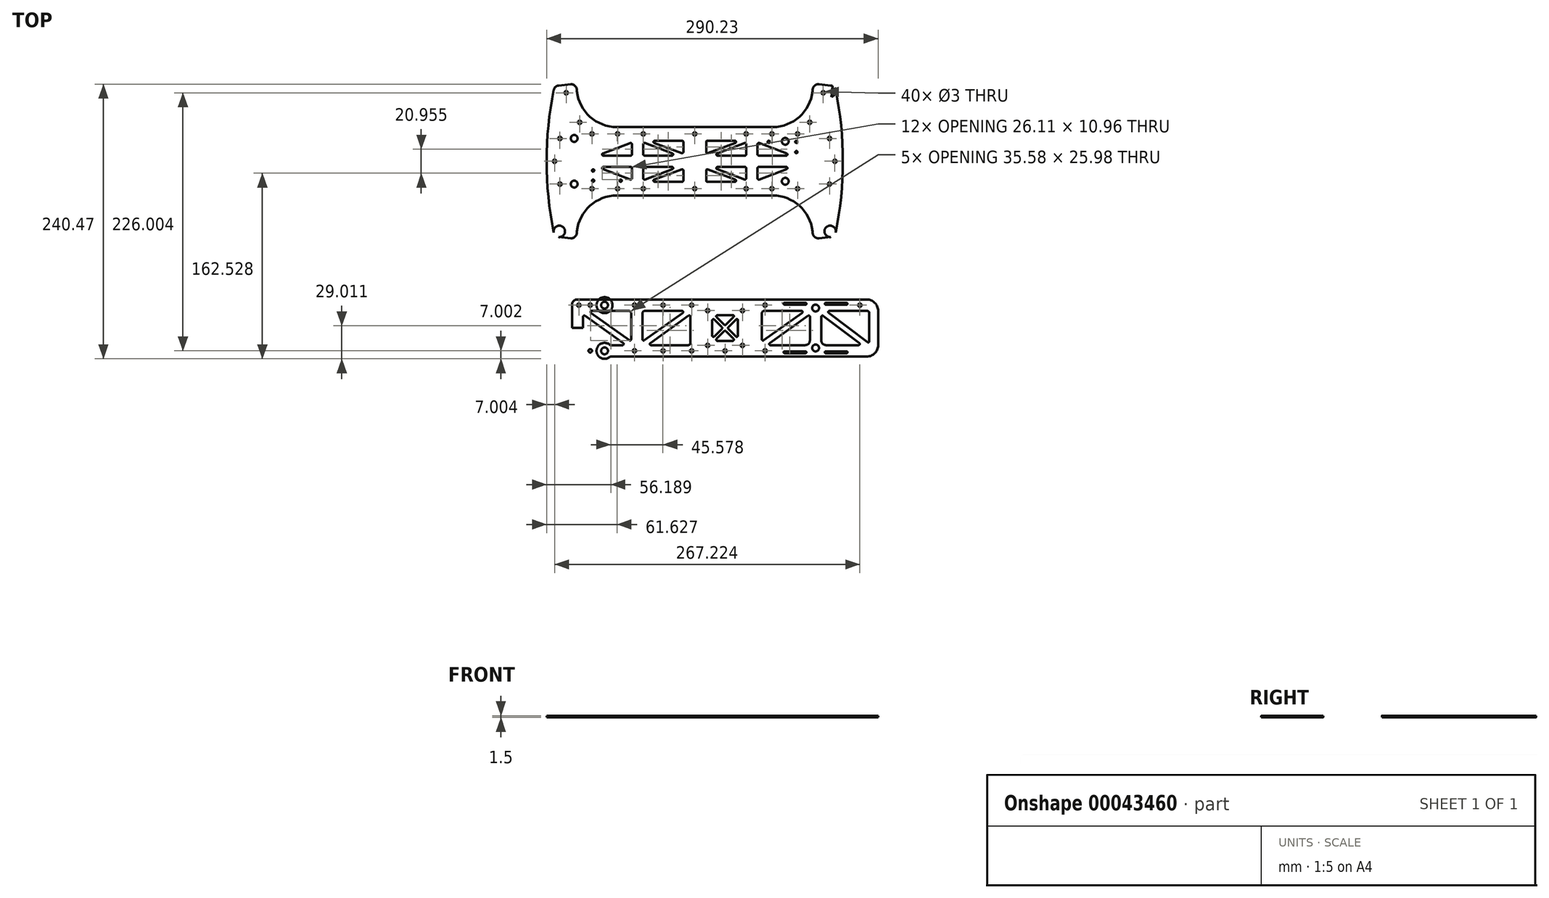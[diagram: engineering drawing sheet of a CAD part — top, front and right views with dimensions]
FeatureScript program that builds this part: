
annotation { "Feature Type Name" : "Feature", "Feature Type Description" : "" }
export const myFeature = defineFeature(function(context is Context, id is Id, definition is map)
    precondition{}
    {
        {
            var Q0;
            Q0=qCreatedBy(makeId("Top.planeOp"),FACE);
            var sketch = newSketch(context, id + "F0", { "sketchPlane" : qUnion([Q0])});
            skLineSegment(sketch, "E0", {"start": v(-133.26, 711.65) * mm, "end": v(112.1, 711.65) * mm});
            skCircle(sketch, "E1", {"center": v(-123.08, 771.65) * mm, "radius": 1.5 * mm});
            skCircle(sketch, "E2", {"center": v(-111.3, 745.73) * mm, "radius": 1.5 * mm});
            skCircle(sketch, "E3", {"center": v(90.15, 745.73) * mm, "radius": 1.5 * mm});
            skCircle(sketch, "E4", {"center": v(101.92, 771.65) * mm, "radius": 1.5 * mm});
            skLineSegment(sketch, "E5", {"start": v(-126.98, 737.05) * mm, "end": v(-131.27, 777.82) * mm});
            skLineSegment(sketch, "E6", {"start": v(-131.27, 777.82) * mm, "end": v(-116.35, 779.4) * mm});
            skLineSegment(sketch, "E7", {"start": v(-116.35, 779.4) * mm, "end": v(-112.06, 738.62) * mm});
            skLineSegment(sketch, "E8", {"start": v(-112.06, 738.62) * mm, "end": v(-126.98, 737.05) * mm});
            skLineSegment(sketch, "E9", {"start": v(-133.26, 777.61) * mm, "end": v(-119.33, 779.08) * mm});
            skLineSegment(sketch, "E10", {"start": v(-133.26, 777.61) * mm, "end": v(-133.26, 711.65) * mm});
            skLineSegment(sketch, "E11", {"start": v(95.2, 779.4) * mm, "end": v(110.11, 777.82) * mm});
            skLineSegment(sketch, "E12", {"start": v(110.11, 777.82) * mm, "end": v(105.83, 737.05) * mm});
            skLineSegment(sketch, "E13", {"start": v(105.83, 737.05) * mm, "end": v(90.91, 738.62) * mm});
            skLineSegment(sketch, "E14", {"start": v(90.91, 738.62) * mm, "end": v(95.2, 779.4) * mm});
            skLineSegment(sketch, "E15", {"start": v(98.18, 779.08) * mm, "end": v(112.1, 777.61) * mm});
            skLineSegment(sketch, "E16", {"start": v(112.1, 777.61) * mm, "end": v(112.1, 711.65) * mm});
            skLineSegment(sketch, "E17", {"start": v(-78.86, 741.65) * mm, "end": v(57.7, 741.65) * mm});
            skLineSegment(sketch, "E18", {"start": v(-113.84, 774.63) * mm, "end": v(-113.66, 772.99) * mm});
            skLineSegment(sketch, "E19", {"start": v(92.69, 774.63) * mm, "end": v(92.51, 772.99) * mm});
            skPoint(sketch, "E20.visualSharp", {"position": v(-110.37, 741.65) * mm});
            skArc(sketch, "E20.filletArc", {"start": v(-113.66, 772.99) * mm, "mid": v(-102.28, 750.64) * mm, "end": v(-78.86, 741.65) * mm});
            skPoint(sketch, "E21.visualSharp", {"position": v(89.22, 741.65) * mm});
            skArc(sketch, "E21.filletArc", {"start": v(57.7, 741.65) * mm, "mid": v(81.12, 750.64) * mm, "end": v(92.51, 772.99) * mm});
            skLineSegment(sketch, "E22.MirrorCS", {"start": v(-131.27, 645.47) * mm, "end": v(-116.35, 643.9) * mm});
            skLineSegment(sketch, "E23.MirrorCS", {"start": v(92.69, 648.66) * mm, "end": v(92.51, 650.3) * mm});
            skLineSegment(sketch, "E24.MirrorCS", {"start": v(-113.84, 648.66) * mm, "end": v(-113.66, 650.3) * mm});
            skLineSegment(sketch, "E25.MirrorCS", {"start": v(-133.26, 645.68) * mm, "end": v(-119.33, 644.21) * mm});
            skCircle(sketch, "E26.MirrorC", {"center": v(-123.08, 651.65) * mm, "radius": 1.5 * mm});
            skCircle(sketch, "E27.MirrorC", {"center": v(90.15, 677.56) * mm, "radius": 1.5 * mm});
            skCircle(sketch, "E28.MirrorC", {"center": v(-111.3, 677.56) * mm, "radius": 1.5 * mm});
            skLineSegment(sketch, "E29.MirrorCS", {"start": v(98.18, 644.21) * mm, "end": v(112.1, 645.68) * mm});
            skCircle(sketch, "E30.MirrorC", {"center": v(101.92, 651.65) * mm, "radius": 1.5 * mm});
            skPoint(sketch, "E31.MirrorP", {"position": v(-110.37, 681.65) * mm});
            skPoint(sketch, "E32.MirrorP", {"position": v(89.22, 681.65) * mm});
            skLineSegment(sketch, "E33.MirrorCS", {"start": v(110.11, 645.47) * mm, "end": v(105.83, 686.24) * mm});
            skLineSegment(sketch, "E34.MirrorCS", {"start": v(95.2, 643.9) * mm, "end": v(110.11, 645.47) * mm});
            skLineSegment(sketch, "E35.MirrorCS", {"start": v(-133.26, 645.68) * mm, "end": v(-133.26, 711.65) * mm});
            skLineSegment(sketch, "E36.MirrorCS", {"start": v(90.91, 684.68) * mm, "end": v(95.2, 643.9) * mm});
            skLineSegment(sketch, "E37.MirrorCS", {"start": v(-126.98, 686.24) * mm, "end": v(-131.27, 645.47) * mm});
            skLineSegment(sketch, "E38.MirrorCS", {"start": v(-78.86, 681.65) * mm, "end": v(57.7, 681.65) * mm});
            skLineSegment(sketch, "E39.MirrorCS", {"start": v(-116.35, 643.9) * mm, "end": v(-112.06, 684.68) * mm});
            skArc(sketch, "E40.MirrorCS", {"start": v(57.7, 681.65) * mm, "mid": v(81.12, 672.66) * mm, "end": v(92.51, 650.3) * mm});
            skLineSegment(sketch, "E41.MirrorCS", {"start": v(105.83, 686.24) * mm, "end": v(90.91, 684.68) * mm});
            skLineSegment(sketch, "E42.MirrorCS", {"start": v(-112.06, 684.68) * mm, "end": v(-126.98, 686.24) * mm});
            skLineSegment(sketch, "E43.MirrorCS", {"start": v(112.1, 645.68) * mm, "end": v(112.1, 711.65) * mm});
            skLineSegment(sketch, "E44", {"start": v(-10.58, 741.65) * mm, "end": v(-10.58, 681.65) * mm});
            skPoint(sketch, "E45.visualSharp", {"position": v(-133.26, 777.61) * mm});
            skPoint(sketch, "E46.visualSharp", {"position": v(-114.36, 779.6) * mm});
            skArc(sketch, "E46.filletArc", {"start": v(-113.84, 774.63) * mm, "mid": v(-115.66, 778) * mm, "end": v(-119.33, 779.08) * mm});
            skPoint(sketch, "E47.visualSharp", {"position": v(93.2, 779.6) * mm});
            skArc(sketch, "E47.filletArc", {"start": v(98.18, 779.08) * mm, "mid": v(94.51, 778) * mm, "end": v(92.69, 774.63) * mm});
            skPoint(sketch, "E48.visualSharp", {"position": v(112.1, 777.61) * mm});
            skPoint(sketch, "E49.visualSharp", {"position": v(-133.26, 645.68) * mm});
            skPoint(sketch, "E50.visualSharp", {"position": v(-114.36, 643.7) * mm});
            skArc(sketch, "E50.filletArc", {"start": v(-119.33, 644.21) * mm, "mid": v(-115.66, 645.3) * mm, "end": v(-113.84, 648.66) * mm});
            skPoint(sketch, "E51.visualSharp", {"position": v(93.2, 643.7) * mm});
            skArc(sketch, "E51.filletArc", {"start": v(92.69, 648.66) * mm, "mid": v(94.51, 645.3) * mm, "end": v(98.18, 644.21) * mm});
            skPoint(sketch, "E52.visualSharp", {"position": v(112.1, 645.68) * mm});
            skLineSegment(sketch, "E53", {"start": v(-122.32, 682.74) * mm, "end": v(-117.35, 682.21) * mm});
            skLineSegment(sketch, "E54", {"start": v(-115.57, 680.02) * mm, "end": v(-117.5, 661.62) * mm});
            skLineSegment(sketch, "E55", {"start": v(-119.7, 659.84) * mm, "end": v(-124.67, 660.36) * mm});
            skLineSegment(sketch, "E56", {"start": v(-126.45, 662.56) * mm, "end": v(-124.52, 680.96) * mm});
            skLineSegment(sketch, "E57.MirrorCS", {"start": v(101.17, 682.74) * mm, "end": v(96.2, 682.21) * mm});
            skLineSegment(sketch, "E58.MirrorCS", {"start": v(105.3, 662.56) * mm, "end": v(103.37, 680.96) * mm});
            skLineSegment(sketch, "E59.MirrorCS", {"start": v(98.55, 659.84) * mm, "end": v(103.52, 660.36) * mm});
            skLineSegment(sketch, "E60.MirrorCS", {"start": v(94.42, 680.02) * mm, "end": v(96.35, 661.62) * mm});
            skLineSegment(sketch, "E61.MirrorCS", {"start": v(101.17, 740.55) * mm, "end": v(96.2, 741.08) * mm});
            skLineSegment(sketch, "E62.MirrorCS", {"start": v(94.42, 743.27) * mm, "end": v(96.35, 761.67) * mm});
            skLineSegment(sketch, "E63.MirrorCS", {"start": v(105.3, 760.73) * mm, "end": v(103.37, 742.33) * mm});
            skLineSegment(sketch, "E64.MirrorCS", {"start": v(98.55, 763.45) * mm, "end": v(103.52, 762.93) * mm});
            skLineSegment(sketch, "E65.MirrorCS", {"start": v(-122.32, 740.55) * mm, "end": v(-117.35, 741.08) * mm});
            skLineSegment(sketch, "E66.MirrorCS", {"start": v(-126.45, 760.73) * mm, "end": v(-124.52, 742.33) * mm});
            skLineSegment(sketch, "E67.MirrorCS", {"start": v(-115.57, 743.27) * mm, "end": v(-117.5, 761.67) * mm});
            skLineSegment(sketch, "E68.MirrorCS", {"start": v(-119.7, 763.45) * mm, "end": v(-124.67, 762.93) * mm});
            skCircle(sketch, "E69", {"center": v(-10.58, 735.65) * mm, "radius": 1.5 * mm});
            skCircle(sketch, "E70", {"center": v(-55.58, 735.65) * mm, "radius": 1.5 * mm});
            skCircle(sketch, "E71", {"center": v(-100.58, 735.65) * mm, "radius": 1.5 * mm});
            skCircle(sketch, "E72.MirrorC", {"center": v(34.42, 735.65) * mm, "radius": 1.5 * mm});
            skCircle(sketch, "E73.MirrorC", {"center": v(79.42, 735.65) * mm, "radius": 1.5 * mm});
            skCircle(sketch, "E74.MirrorC", {"center": v(-55.58, 687.65) * mm, "radius": 1.5 * mm});
            skCircle(sketch, "E75.MirrorC", {"center": v(-10.58, 687.65) * mm, "radius": 1.5 * mm});
            skCircle(sketch, "E76.MirrorC", {"center": v(34.42, 687.65) * mm, "radius": 1.5 * mm});
            skCircle(sketch, "E77.MirrorC", {"center": v(79.42, 687.65) * mm, "radius": 1.5 * mm});
            skCircle(sketch, "E78.MirrorC", {"center": v(-100.58, 687.65) * mm, "radius": 1.5 * mm});
            skCircle(sketch, "E79", {"center": v(-133.26, 711.65) * mm, "radius": 1.5 * mm});
            skCircle(sketch, "E80.MirrorC", {"center": v(112.1, 711.65) * mm, "radius": 1.5 * mm});
            skCircle(sketch, "E81", {"center": v(-128.58, 731.65) * mm, "radius": 1.5 * mm});
            skCircle(sketch, "E82.MirrorC", {"center": v(-128.58, 691.65) * mm, "radius": 1.5 * mm});
            skCircle(sketch, "E83.MirrorC", {"center": v(107.42, 731.65) * mm, "radius": 1.5 * mm});
            skCircle(sketch, "E84.MirrorC", {"center": v(107.42, 691.65) * mm, "radius": 1.5 * mm});
            skLineSegment(sketch, "E85.bottom", {"start": v(-20.58, 716.65) * mm, "end": v(-55.58, 716.65) * mm});
            skLineSegment(sketch, "E85.top", {"start": v(-20.58, 729.65) * mm, "end": v(-55.58, 729.65) * mm});
            skLineSegment(sketch, "E85.left", {"start": v(-20.58, 716.65) * mm, "end": v(-20.58, 729.65) * mm});
            skLineSegment(sketch, "E85.right", {"start": v(-55.58, 716.65) * mm, "end": v(-55.58, 729.65) * mm});
            skLineSegment(sketch, "E86.bottom", {"start": v(-65.58, 716.65) * mm, "end": v(-100.58, 716.65) * mm});
            skLineSegment(sketch, "E86.top", {"start": v(-65.58, 729.65) * mm, "end": v(-100.58, 729.65) * mm});
            skLineSegment(sketch, "E86.left", {"start": v(-65.58, 716.65) * mm, "end": v(-65.58, 729.65) * mm});
            skLineSegment(sketch, "E86.right", {"start": v(-100.58, 716.65) * mm, "end": v(-100.58, 729.65) * mm});
            skLineSegment(sketch, "E87.MirrorCS", {"start": v(44.42, 716.65) * mm, "end": v(79.42, 716.65) * mm});
            skLineSegment(sketch, "E88.MirrorCS", {"start": v(-0.58, 716.65) * mm, "end": v(-0.58, 729.65) * mm});
            skLineSegment(sketch, "E89.MirrorCS", {"start": v(-0.58, 729.65) * mm, "end": v(34.42, 729.65) * mm});
            skLineSegment(sketch, "E90.MirrorCS", {"start": v(-0.58, 716.65) * mm, "end": v(34.42, 716.65) * mm});
            skLineSegment(sketch, "E91.MirrorCS", {"start": v(44.42, 729.65) * mm, "end": v(79.42, 729.65) * mm});
            skLineSegment(sketch, "E92.MirrorCS", {"start": v(34.42, 716.65) * mm, "end": v(34.42, 729.65) * mm});
            skLineSegment(sketch, "E93.MirrorCS", {"start": v(44.42, 716.65) * mm, "end": v(44.42, 729.65) * mm});
            skLineSegment(sketch, "E94.MirrorCS", {"start": v(79.42, 716.65) * mm, "end": v(79.42, 729.65) * mm});
            skLineSegment(sketch, "E95.MirrorCS", {"start": v(-65.58, 706.65) * mm, "end": v(-100.58, 706.65) * mm});
            skLineSegment(sketch, "E96.MirrorCS", {"start": v(-20.58, 706.65) * mm, "end": v(-55.58, 706.65) * mm});
            skLineSegment(sketch, "E97.MirrorCS", {"start": v(-20.58, 693.65) * mm, "end": v(-55.58, 693.65) * mm});
            skLineSegment(sketch, "E98.MirrorCS", {"start": v(-20.58, 706.65) * mm, "end": v(-20.58, 693.65) * mm});
            skLineSegment(sketch, "E99.MirrorCS", {"start": v(-55.58, 706.65) * mm, "end": v(-55.58, 693.65) * mm});
            skLineSegment(sketch, "E100.MirrorCS", {"start": v(-65.58, 693.65) * mm, "end": v(-100.58, 693.65) * mm});
            skLineSegment(sketch, "E101.MirrorCS", {"start": v(-65.58, 706.65) * mm, "end": v(-65.58, 693.65) * mm});
            skLineSegment(sketch, "E102.MirrorCS", {"start": v(-100.58, 706.65) * mm, "end": v(-100.58, 693.65) * mm});
            skLineSegment(sketch, "E103.MirrorCS", {"start": v(79.42, 706.65) * mm, "end": v(79.42, 693.65) * mm});
            skLineSegment(sketch, "E104.MirrorCS", {"start": v(-0.58, 706.65) * mm, "end": v(34.42, 706.65) * mm});
            skLineSegment(sketch, "E105.MirrorCS", {"start": v(44.42, 706.65) * mm, "end": v(44.42, 693.65) * mm});
            skLineSegment(sketch, "E106.MirrorCS", {"start": v(-0.58, 693.65) * mm, "end": v(34.42, 693.65) * mm});
            skLineSegment(sketch, "E107.MirrorCS", {"start": v(44.42, 693.65) * mm, "end": v(79.42, 693.65) * mm});
            skLineSegment(sketch, "E108.MirrorCS", {"start": v(44.42, 706.65) * mm, "end": v(79.42, 706.65) * mm});
            skLineSegment(sketch, "E109.MirrorCS", {"start": v(-0.58, 706.65) * mm, "end": v(-0.58, 693.65) * mm});
            skLineSegment(sketch, "E110.MirrorCS", {"start": v(34.42, 706.65) * mm, "end": v(34.42, 693.65) * mm});
            skLineSegment(sketch, "E111", {"start": v(-55.58, 729.65) * mm, "end": v(-20.58, 716.65) * mm});
            skLineSegment(sketch, "E112", {"start": v(-51.27, 729.65) * mm, "end": v(-20.58, 718.25) * mm});
            skLineSegment(sketch, "E113", {"start": v(-55.58, 728.05) * mm, "end": v(-24.88, 716.65) * mm});
            skLineSegment(sketch, "E114", {"start": v(-65.58, 729.65) * mm, "end": v(-100.58, 716.65) * mm});
            skLineSegment(sketch, "E115", {"start": v(-100.58, 718.25) * mm, "end": v(-69.88, 729.65) * mm});
            skLineSegment(sketch, "E116", {"start": v(-96.27, 716.65) * mm, "end": v(-65.58, 728.05) * mm});
            skLineSegment(sketch, "E117.MirrorCS", {"start": v(-51.27, 693.65) * mm, "end": v(-20.58, 705.05) * mm});
            skLineSegment(sketch, "E118.MirrorCS", {"start": v(-55.58, 693.65) * mm, "end": v(-20.58, 706.65) * mm});
            skLineSegment(sketch, "E119.MirrorCS", {"start": v(-55.58, 695.25) * mm, "end": v(-24.88, 706.65) * mm});
            skLineSegment(sketch, "E120.MirrorCS", {"start": v(-100.58, 705.05) * mm, "end": v(-69.88, 693.65) * mm});
            skLineSegment(sketch, "E121.MirrorCS", {"start": v(-65.58, 693.65) * mm, "end": v(-100.58, 706.65) * mm});
            skLineSegment(sketch, "E122.MirrorCS", {"start": v(-96.27, 706.65) * mm, "end": v(-65.58, 695.25) * mm});
            skLineSegment(sketch, "E123.MirrorCS", {"start": v(30.12, 729.65) * mm, "end": v(-0.58, 718.25) * mm});
            skLineSegment(sketch, "E124.MirrorCS", {"start": v(34.42, 728.05) * mm, "end": v(3.73, 716.65) * mm});
            skLineSegment(sketch, "E125.MirrorCS", {"start": v(34.42, 729.65) * mm, "end": v(-0.58, 716.65) * mm});
            skLineSegment(sketch, "E126.MirrorCS", {"start": v(34.42, 693.65) * mm, "end": v(-0.58, 706.65) * mm});
            skLineSegment(sketch, "E127.MirrorCS", {"start": v(34.42, 695.25) * mm, "end": v(3.73, 706.65) * mm});
            skLineSegment(sketch, "E128.MirrorCS", {"start": v(30.12, 693.65) * mm, "end": v(-0.58, 705.05) * mm});
            skLineSegment(sketch, "E129.MirrorCS", {"start": v(44.42, 729.65) * mm, "end": v(79.42, 716.65) * mm});
            skLineSegment(sketch, "E130.MirrorCS", {"start": v(75.12, 716.65) * mm, "end": v(44.42, 728.05) * mm});
            skLineSegment(sketch, "E131.MirrorCS", {"start": v(79.42, 718.25) * mm, "end": v(48.73, 729.65) * mm});
            skLineSegment(sketch, "E132.MirrorCS", {"start": v(44.42, 693.65) * mm, "end": v(79.42, 706.65) * mm});
            skLineSegment(sketch, "E133.MirrorCS", {"start": v(79.42, 705.05) * mm, "end": v(48.73, 693.65) * mm});
            skLineSegment(sketch, "E134.MirrorCS", {"start": v(75.12, 706.65) * mm, "end": v(44.42, 695.25) * mm});
            skCircle(sketch, "E135", {"center": v(-99.58, 728.65) * mm, "radius": 1 * mm});
            skCircle(sketch, "E136", {"center": v(-99.58, 719.68) * mm, "radius": 1 * mm});
            skCircle(sketch, "E137", {"center": v(-75.45, 728.65) * mm, "radius": 1 * mm});
            skCircle(sketch, "E138", {"center": v(-66.58, 726.6) * mm, "radius": 1 * mm});
            skCircle(sketch, "E139", {"center": v(-90.7, 717.65) * mm, "radius": 1 * mm});
            skCircle(sketch, "E140", {"center": v(-66.58, 717.65) * mm, "radius": 1 * mm});
            skCircle(sketch, "E141", {"center": v(-54.58, 717.65) * mm, "radius": 1 * mm});
            skCircle(sketch, "E142", {"center": v(-45.7, 728.65) * mm, "radius": 1 * mm});
            skCircle(sketch, "E143", {"center": v(-21.58, 728.65) * mm, "radius": 1 * mm});
            skCircle(sketch, "E144", {"center": v(-21.58, 719.68) * mm, "radius": 1 * mm});
            skCircle(sketch, "E145", {"center": v(-30.45, 717.65) * mm, "radius": 1 * mm});
            skCircle(sketch, "E146", {"center": v(-54.58, 726.6) * mm, "radius": 1 * mm});
            skCircle(sketch, "E147.MirrorC", {"center": v(-99.58, 694.65) * mm, "radius": 1 * mm});
            skCircle(sketch, "E148.MirrorC", {"center": v(-99.58, 703.6) * mm, "radius": 1 * mm});
            skCircle(sketch, "E149.MirrorC", {"center": v(-90.7, 705.65) * mm, "radius": 1 * mm});
            skCircle(sketch, "E150.MirrorC", {"center": v(-75.45, 694.65) * mm, "radius": 1 * mm});
            skCircle(sketch, "E151.MirrorC", {"center": v(-66.58, 696.68) * mm, "radius": 1 * mm});
            skCircle(sketch, "E152.MirrorC", {"center": v(-66.58, 705.65) * mm, "radius": 1 * mm});
            skCircle(sketch, "E153.MirrorC", {"center": v(-54.58, 696.68) * mm, "radius": 1 * mm});
            skCircle(sketch, "E154.MirrorC", {"center": v(-54.58, 705.65) * mm, "radius": 1 * mm});
            skCircle(sketch, "E155.MirrorC", {"center": v(-45.7, 694.65) * mm, "radius": 1 * mm});
            skCircle(sketch, "E156.MirrorC", {"center": v(-30.45, 705.65) * mm, "radius": 1 * mm});
            skCircle(sketch, "E157.MirrorC", {"center": v(-21.58, 703.6) * mm, "radius": 1 * mm});
            skCircle(sketch, "E158.MirrorC", {"center": v(-21.58, 694.65) * mm, "radius": 1 * mm});
            skCircle(sketch, "E159.MirrorC", {"center": v(0.42, 719.68) * mm, "radius": 1 * mm});
            skCircle(sketch, "E160.MirrorC", {"center": v(0.42, 728.65) * mm, "radius": 1 * mm});
            skCircle(sketch, "E161.MirrorC", {"center": v(24.55, 728.65) * mm, "radius": 1 * mm});
            skCircle(sketch, "E162.MirrorC", {"center": v(33.42, 726.6) * mm, "radius": 1 * mm});
            skCircle(sketch, "E163.MirrorC", {"center": v(33.42, 717.65) * mm, "radius": 1 * mm});
            skCircle(sketch, "E164.MirrorC", {"center": v(9.3, 717.65) * mm, "radius": 1 * mm});
            skCircle(sketch, "E165.MirrorC", {"center": v(9.3, 705.65) * mm, "radius": 1 * mm});
            skCircle(sketch, "E166.MirrorC", {"center": v(33.42, 705.65) * mm, "radius": 1 * mm});
            skCircle(sketch, "E167.MirrorC", {"center": v(33.42, 696.68) * mm, "radius": 1 * mm});
            skCircle(sketch, "E168.MirrorC", {"center": v(24.55, 694.65) * mm, "radius": 1 * mm});
            skCircle(sketch, "E169.MirrorC", {"center": v(0.42, 694.65) * mm, "radius": 1 * mm});
            skCircle(sketch, "E170.MirrorC", {"center": v(0.42, 703.6) * mm, "radius": 1 * mm});
            skCircle(sketch, "E171.MirrorC", {"center": v(54.3, 728.65) * mm, "radius": 1 * mm});
            skCircle(sketch, "E172.MirrorC", {"center": v(45.42, 726.6) * mm, "radius": 1 * mm});
            skCircle(sketch, "E173.MirrorC", {"center": v(45.42, 717.65) * mm, "radius": 1 * mm});
            skCircle(sketch, "E174.MirrorC", {"center": v(69.55, 717.65) * mm, "radius": 1 * mm});
            skCircle(sketch, "E175.MirrorC", {"center": v(78.42, 719.68) * mm, "radius": 1 * mm});
            skCircle(sketch, "E176.MirrorC", {"center": v(78.42, 728.65) * mm, "radius": 1 * mm});
            skCircle(sketch, "E177.MirrorC", {"center": v(69.55, 705.65) * mm, "radius": 1 * mm});
            skCircle(sketch, "E178.MirrorC", {"center": v(45.42, 705.65) * mm, "radius": 1 * mm});
            skCircle(sketch, "E179.MirrorC", {"center": v(45.42, 696.68) * mm, "radius": 1 * mm});
            skCircle(sketch, "E180.MirrorC", {"center": v(54.3, 694.65) * mm, "radius": 1 * mm});
            skCircle(sketch, "E181.MirrorC", {"center": v(78.42, 703.6) * mm, "radius": 1 * mm});
            skCircle(sketch, "E182.MirrorC", {"center": v(78.42, 694.65) * mm, "radius": 1 * mm});
            skCircle(sketch, "E183", {"center": v(-116.08, 691.65) * mm, "radius": 3 * mm});
            skCircle(sketch, "E184.MirrorC", {"center": v(-116.08, 731.65) * mm, "radius": 3 * mm});
            skCircle(sketch, "E185", {"center": v(68.67, 729.15) * mm, "radius": 3 * mm});
            skCircle(sketch, "E186.MirrorC", {"center": v(68.67, 694.15) * mm, "radius": 3 * mm});
            skPoint(sketch, "E187.visualSharp", {"position": v(-126.66, 762.72) * mm});
            skArc(sketch, "E187.filletArc", {"start": v(-124.67, 762.93) * mm, "mid": v(-126.02, 762.2) * mm, "end": v(-126.45, 760.73) * mm});
            skPoint(sketch, "E188.visualSharp", {"position": v(-117.71, 763.66) * mm});
            skArc(sketch, "E188.filletArc", {"start": v(-117.5, 761.67) * mm, "mid": v(-118.23, 763.02) * mm, "end": v(-119.7, 763.45) * mm});
            skPoint(sketch, "E189.visualSharp", {"position": v(-115.36, 741.29) * mm});
            skArc(sketch, "E189.filletArc", {"start": v(-117.35, 741.08) * mm, "mid": v(-116, 741.8) * mm, "end": v(-115.57, 743.27) * mm});
            skPoint(sketch, "E190.visualSharp", {"position": v(-124.31, 740.35) * mm});
            skArc(sketch, "E190.filletArc", {"start": v(-124.52, 742.33) * mm, "mid": v(-123.79, 740.99) * mm, "end": v(-122.32, 740.55) * mm});
            skPoint(sketch, "E191.visualSharp", {"position": v(-124.31, 682.95) * mm});
            skArc(sketch, "E191.filletArc", {"start": v(-122.32, 682.74) * mm, "mid": v(-123.79, 682.3) * mm, "end": v(-124.52, 680.96) * mm});
            skPoint(sketch, "E192.visualSharp", {"position": v(-117.71, 659.63) * mm});
            skArc(sketch, "E192.filletArc", {"start": v(-119.7, 659.84) * mm, "mid": v(-118.23, 660.27) * mm, "end": v(-117.5, 661.62) * mm});
            skPoint(sketch, "E193.visualSharp", {"position": v(-115.36, 682) * mm});
            skArc(sketch, "E193.filletArc", {"start": v(-115.57, 680.02) * mm, "mid": v(-116, 681.48) * mm, "end": v(-117.35, 682.21) * mm});
            skPoint(sketch, "E194.visualSharp", {"position": v(-126.66, 660.57) * mm});
            skArc(sketch, "E194.filletArc", {"start": v(-126.45, 662.56) * mm, "mid": v(-126.02, 661.1) * mm, "end": v(-124.67, 660.36) * mm});
            skPoint(sketch, "E195.visualSharp", {"position": v(94.2, 682) * mm});
            skArc(sketch, "E195.filletArc", {"start": v(96.2, 682.21) * mm, "mid": v(94.85, 681.48) * mm, "end": v(94.42, 680.02) * mm});
            skPoint(sketch, "E196.visualSharp", {"position": v(103.16, 682.95) * mm});
            skArc(sketch, "E196.filletArc", {"start": v(103.37, 680.96) * mm, "mid": v(102.64, 682.3) * mm, "end": v(101.17, 682.74) * mm});
            skPoint(sketch, "E197.visualSharp", {"position": v(105.51, 660.57) * mm});
            skArc(sketch, "E197.filletArc", {"start": v(103.52, 660.36) * mm, "mid": v(104.87, 661.1) * mm, "end": v(105.3, 662.56) * mm});
            skPoint(sketch, "E198.visualSharp", {"position": v(96.56, 659.63) * mm});
            skArc(sketch, "E198.filletArc", {"start": v(96.35, 661.62) * mm, "mid": v(97.08, 660.27) * mm, "end": v(98.55, 659.84) * mm});
            skPoint(sketch, "E199.visualSharp", {"position": v(105.51, 762.72) * mm});
            skArc(sketch, "E199.filletArc", {"start": v(105.3, 760.73) * mm, "mid": v(104.87, 762.2) * mm, "end": v(103.52, 762.93) * mm});
            skPoint(sketch, "E200.visualSharp", {"position": v(103.16, 740.35) * mm});
            skArc(sketch, "E200.filletArc", {"start": v(101.17, 740.55) * mm, "mid": v(102.64, 740.99) * mm, "end": v(103.37, 742.33) * mm});
            skPoint(sketch, "E201.visualSharp", {"position": v(96.56, 763.66) * mm});
            skArc(sketch, "E201.filletArc", {"start": v(98.55, 763.45) * mm, "mid": v(97.08, 763.02) * mm, "end": v(96.35, 761.67) * mm});
            skPoint(sketch, "E202.visualSharp", {"position": v(94.2, 741.29) * mm});
            skArc(sketch, "E202.filletArc", {"start": v(94.42, 743.27) * mm, "mid": v(94.85, 741.8) * mm, "end": v(96.2, 741.08) * mm});
            skCircle(sketch, "E203", {"center": v(-78.08, 735.65) * mm, "radius": 1.5 * mm});
            skCircle(sketch, "E204.MirrorC", {"center": v(56.92, 735.65) * mm, "radius": 1.5 * mm});
            skCircle(sketch, "E205.MirrorC", {"center": v(-78.08, 687.65) * mm, "radius": 1.5 * mm});
            skCircle(sketch, "E206.MirrorC", {"center": v(56.92, 687.65) * mm, "radius": 1.5 * mm});
            skArc(sketch, "E207", {"start": v(-78.86, 681.65) * mm, "mid": v(-102.28, 672.66) * mm, "end": v(-113.66, 650.3) * mm});
            skArc(sketch, "E208", {"start": v(-133.26, 777.61) * mm, "mid": v(-140.26, 711.65) * mm, "end": v(-133.26, 645.68) * mm});
            skCircle(sketch, "E209", {"center": v(-129.1, 773.02) * mm, "radius": 5 * mm});
            skCircle(sketch, "E210", {"center": v(-129.1, 650.27) * mm, "radius": 5 * mm});
            skArc(sketch, "E211", {"start": v(112.1, 645.68) * mm, "mid": v(119.1, 711.65) * mm, "end": v(112.1, 777.61) * mm});
            skCircle(sketch, "E212", {"center": v(107.95, 773.02) * mm, "radius": 5 * mm});
            skCircle(sketch, "E213", {"center": v(107.95, 650.27) * mm, "radius": 5 * mm});
            skSolve(sketch);
        }
        {
            var Q0;
            {var subQ52=sQuery(id+"F0.wireOp",EDGE,"E3");Q0=makeQuery(id+"F0.imprint","IMPRINT",FACE,{"disambiguationData":[TD([[makeQuery(id+"F0.imprint","IMPRINT",EDGE,{"derivedFrom":subQ52}),-1.0]])]});}
            var Q1;
            {var subQ43=sQuery(id+"F0.wireOp",EDGE,"E2");Q1=makeQuery(id+"F0.imprint","IMPRINT",FACE,{"disambiguationData":[TD([[makeQuery(id+"F0.imprint","IMPRINT",EDGE,{"derivedFrom":subQ43}),-1.0]])]});}
            var Q2;
            {var subQ4=sQuery(id+"F0.wireOp",EDGE,"E114");Q2=makeQuery(id+"F0.imprint","IMPRINT",FACE,{"disambiguationData":[TD([[makeQuery(id+"F0.imprint","IMPRINT",EDGE,{"derivedFrom":subQ4}),1.0]])]});}
            var Q3;
            {var subQ5=sQuery(id+"F0.wireOp",EDGE,"E114");Q3=makeQuery(id+"F0.imprint","IMPRINT",FACE,{"disambiguationData":[TD([[makeQuery(id+"F0.imprint","IMPRINT",EDGE,{"derivedFrom":subQ5}),-1.0]])]});}
            var Q4;
            {var subQ4=sQuery(id+"F0.wireOp",EDGE,"E121.MirrorCS");Q4=makeQuery(id+"F0.imprint","IMPRINT",FACE,{"disambiguationData":[TD([[makeQuery(id+"F0.imprint","IMPRINT",EDGE,{"derivedFrom":subQ4}),-1.0]])]});}
            var Q5;
            {var subQ5=sQuery(id+"F0.wireOp",EDGE,"E121.MirrorCS");Q5=makeQuery(id+"F0.imprint","IMPRINT",FACE,{"disambiguationData":[TD([[makeQuery(id+"F0.imprint","IMPRINT",EDGE,{"derivedFrom":subQ5}),1.0]])]});}
            var Q6;
            {var subQ4=sQuery(id+"F0.wireOp",EDGE,"E118.MirrorCS");Q6=makeQuery(id+"F0.imprint","IMPRINT",FACE,{"disambiguationData":[TD([[makeQuery(id+"F0.imprint","IMPRINT",EDGE,{"derivedFrom":subQ4}),1.0]])]});}
            var Q7;
            {var subQ3=sQuery(id+"F0.wireOp",EDGE,"E118.MirrorCS");Q7=makeQuery(id+"F0.imprint","IMPRINT",FACE,{"disambiguationData":[TD([[makeQuery(id+"F0.imprint","IMPRINT",EDGE,{"derivedFrom":subQ3}),-1.0]])]});}
            var Q8;
            {var subQ4=sQuery(id+"F0.wireOp",EDGE,"E111");Q8=makeQuery(id+"F0.imprint","IMPRINT",FACE,{"disambiguationData":[TD([[makeQuery(id+"F0.imprint","IMPRINT",EDGE,{"derivedFrom":subQ4}),-1.0]])]});}
            var Q9;
            {var subQ4=sQuery(id+"F0.wireOp",EDGE,"E111");Q9=makeQuery(id+"F0.imprint","IMPRINT",FACE,{"disambiguationData":[TD([[makeQuery(id+"F0.imprint","IMPRINT",EDGE,{"derivedFrom":subQ4}),1.0]])]});}
            var Q10;
            {var subQ5=sQuery(id+"F0.wireOp",EDGE,"E125.MirrorCS");Q10=makeQuery(id+"F0.imprint","IMPRINT",FACE,{"disambiguationData":[TD([[makeQuery(id+"F0.imprint","IMPRINT",EDGE,{"derivedFrom":subQ5}),-1.0]])]});}
            var Q11;
            {var subQ5=sQuery(id+"F0.wireOp",EDGE,"E125.MirrorCS");Q11=makeQuery(id+"F0.imprint","IMPRINT",FACE,{"disambiguationData":[TD([[makeQuery(id+"F0.imprint","IMPRINT",EDGE,{"derivedFrom":subQ5}),1.0]])]});}
            var Q12;
            {var subQ4=sQuery(id+"F0.wireOp",EDGE,"E126.MirrorCS");Q12=makeQuery(id+"F0.imprint","IMPRINT",FACE,{"disambiguationData":[TD([[makeQuery(id+"F0.imprint","IMPRINT",EDGE,{"derivedFrom":subQ4}),-1.0]])]});}
            var Q13;
            {var subQ4=sQuery(id+"F0.wireOp",EDGE,"E126.MirrorCS");Q13=makeQuery(id+"F0.imprint","IMPRINT",FACE,{"disambiguationData":[TD([[makeQuery(id+"F0.imprint","IMPRINT",EDGE,{"derivedFrom":subQ4}),1.0]])]});}
            var Q14;
            {var subQ0=sQuery(id+"F0.wireOp",EDGE,"E129.MirrorCS");Q14=makeQuery(id+"F0.imprint","IMPRINT",FACE,{"disambiguationData":[TD([[makeQuery(id+"F0.imprint","IMPRINT",EDGE,{"derivedFrom":subQ0}),-1.0]])]});}
            var Q15;
            {var subQ0=sQuery(id+"F0.wireOp",EDGE,"E129.MirrorCS");Q15=makeQuery(id+"F0.imprint","IMPRINT",FACE,{"disambiguationData":[TD([[makeQuery(id+"F0.imprint","IMPRINT",EDGE,{"derivedFrom":subQ0}),1.0]])]});}
            var Q16;
            {var subQ0=sQuery(id+"F0.wireOp",EDGE,"E132.MirrorCS");Q16=makeQuery(id+"F0.imprint","IMPRINT",FACE,{"disambiguationData":[TD([[makeQuery(id+"F0.imprint","IMPRINT",EDGE,{"derivedFrom":subQ0}),1.0]])]});}
            var Q17;
            {var subQ4=sQuery(id+"F0.wireOp",EDGE,"E132.MirrorCS");Q17=makeQuery(id+"F0.imprint","IMPRINT",FACE,{"disambiguationData":[TD([[makeQuery(id+"F0.imprint","IMPRINT",EDGE,{"derivedFrom":subQ4}),-1.0]])]});}
            var Q18;
            {var subQ0=sQuery(id+"F0.wireOp",EDGE,"E86.right");var subQ1=sQuery(id+"F0.wireOp",EDGE,"E86.top");var subQ2=makeQuery(id+"F0.imprint","INTERSECT",VERTEX,{"derivedFrom":[subQ1,subQ0]});Q18=makeQuery(id+"F0.imprint","IMPRINT",FACE,{"disambiguationData":[TD([[makeQuery(id+"F0.imprint","IMPRINT",EDGE,{"disambiguationData":[TD([[subQ2,1.0]])],"derivedFrom":subQ1}),1.0]])]});}
            var Q19;
            {var subQ0=sQuery(id+"F0.wireOp",EDGE,"E115");var subQ1=sQuery(id+"F0.wireOp",EDGE,"E86.right");var subQ2=makeQuery(id+"F0.imprint","INTERSECT",VERTEX,{"derivedFrom":[subQ1,subQ0]});Q19=makeQuery(id+"F0.imprint","IMPRINT",FACE,{"disambiguationData":[TD([[makeQuery(id+"F0.imprint","IMPRINT",EDGE,{"disambiguationData":[TD([[subQ2,-1.0]])],"derivedFrom":subQ1}),-1.0]])]});}
            var Q20;
            {var subQ0=sQuery(id+"F0.wireOp",EDGE,"E116");var subQ1=sQuery(id+"F0.wireOp",EDGE,"E86.bottom");var subQ2=makeQuery(id+"F0.imprint","INTERSECT",VERTEX,{"derivedFrom":[subQ1,subQ0]});Q20=makeQuery(id+"F0.imprint","IMPRINT",FACE,{"disambiguationData":[TD([[makeQuery(id+"F0.imprint","IMPRINT",EDGE,{"disambiguationData":[TD([[subQ2,1.0]])],"derivedFrom":subQ1}),-1.0]])]});}
            var Q21;
            {var subQ0=sQuery(id+"F0.wireOp",EDGE,"E86.left");var subQ1=sQuery(id+"F0.wireOp",EDGE,"E86.bottom");var subQ2=makeQuery(id+"F0.imprint","INTERSECT",VERTEX,{"derivedFrom":[subQ1,subQ0]});Q21=makeQuery(id+"F0.imprint","IMPRINT",FACE,{"disambiguationData":[TD([[makeQuery(id+"F0.imprint","IMPRINT",EDGE,{"disambiguationData":[TD([[subQ2,-1.0]])],"derivedFrom":subQ1}),-1.0]])]});}
            var Q22;
            {var subQ0=sQuery(id+"F0.wireOp",EDGE,"E116");var subQ1=sQuery(id+"F0.wireOp",EDGE,"E86.left");var subQ2=makeQuery(id+"F0.imprint","INTERSECT",VERTEX,{"derivedFrom":[subQ1,subQ0]});Q22=makeQuery(id+"F0.imprint","IMPRINT",FACE,{"disambiguationData":[TD([[makeQuery(id+"F0.imprint","IMPRINT",EDGE,{"disambiguationData":[TD([[subQ2,1.0]])],"derivedFrom":subQ1}),1.0]])]});}
            var Q23;
            {var subQ0=sQuery(id+"F0.wireOp",EDGE,"E115");var subQ1=sQuery(id+"F0.wireOp",EDGE,"E86.top");var subQ2=makeQuery(id+"F0.imprint","INTERSECT",VERTEX,{"derivedFrom":[subQ1,subQ0]});Q23=makeQuery(id+"F0.imprint","IMPRINT",FACE,{"disambiguationData":[TD([[makeQuery(id+"F0.imprint","IMPRINT",EDGE,{"disambiguationData":[TD([[subQ2,-1.0]])],"derivedFrom":subQ1}),1.0]])]});}
            var Q24;
            {var subQ0=sQuery(id+"F0.wireOp",EDGE,"E113");var subQ1=sQuery(id+"F0.wireOp",EDGE,"E85.right");var subQ2=makeQuery(id+"F0.imprint","INTERSECT",VERTEX,{"derivedFrom":[subQ1,subQ0]});Q24=makeQuery(id+"F0.imprint","IMPRINT",FACE,{"disambiguationData":[TD([[makeQuery(id+"F0.imprint","IMPRINT",EDGE,{"disambiguationData":[TD([[subQ2,1.0]])],"derivedFrom":subQ1}),-1.0]])]});}
            var Q25;
            {var subQ0=sQuery(id+"F0.wireOp",EDGE,"E112");var subQ1=sQuery(id+"F0.wireOp",EDGE,"E85.top");var subQ2=makeQuery(id+"F0.imprint","INTERSECT",VERTEX,{"derivedFrom":[subQ1,subQ0]});Q25=makeQuery(id+"F0.imprint","IMPRINT",FACE,{"disambiguationData":[TD([[makeQuery(id+"F0.imprint","IMPRINT",EDGE,{"disambiguationData":[TD([[subQ2,1.0]])],"derivedFrom":subQ1}),1.0]])]});}
            var Q26;
            {var subQ0=sQuery(id+"F0.wireOp",EDGE,"E85.right");var subQ1=sQuery(id+"F0.wireOp",EDGE,"E85.bottom");var subQ2=makeQuery(id+"F0.imprint","INTERSECT",VERTEX,{"derivedFrom":[subQ1,subQ0]});Q26=makeQuery(id+"F0.imprint","IMPRINT",FACE,{"disambiguationData":[TD([[makeQuery(id+"F0.imprint","IMPRINT",EDGE,{"disambiguationData":[TD([[subQ2,1.0]])],"derivedFrom":subQ1}),-1.0]])]});}
            var Q27;
            {var subQ0=sQuery(id+"F0.wireOp",EDGE,"E113");var subQ1=sQuery(id+"F0.wireOp",EDGE,"E85.bottom");var subQ2=makeQuery(id+"F0.imprint","INTERSECT",VERTEX,{"derivedFrom":[subQ1,subQ0]});Q27=makeQuery(id+"F0.imprint","IMPRINT",FACE,{"disambiguationData":[TD([[makeQuery(id+"F0.imprint","IMPRINT",EDGE,{"disambiguationData":[TD([[subQ2,-1.0]])],"derivedFrom":subQ1}),-1.0]])]});}
            var Q28;
            {var subQ0=sQuery(id+"F0.wireOp",EDGE,"E112");var subQ1=sQuery(id+"F0.wireOp",EDGE,"E85.left");var subQ2=makeQuery(id+"F0.imprint","INTERSECT",VERTEX,{"derivedFrom":[subQ1,subQ0]});Q28=makeQuery(id+"F0.imprint","IMPRINT",FACE,{"disambiguationData":[TD([[makeQuery(id+"F0.imprint","IMPRINT",EDGE,{"disambiguationData":[TD([[subQ2,-1.0]])],"derivedFrom":subQ1}),1.0]])]});}
            var Q29;
            {var subQ0=sQuery(id+"F0.wireOp",EDGE,"E85.left");var subQ1=sQuery(id+"F0.wireOp",EDGE,"E85.top");var subQ2=makeQuery(id+"F0.imprint","INTERSECT",VERTEX,{"derivedFrom":[subQ1,subQ0]});Q29=makeQuery(id+"F0.imprint","IMPRINT",FACE,{"disambiguationData":[TD([[makeQuery(id+"F0.imprint","IMPRINT",EDGE,{"disambiguationData":[TD([[subQ2,-1.0]])],"derivedFrom":subQ1}),1.0]])]});}
            var Q30;
            {var subQ0=sQuery(id+"F0.wireOp",EDGE,"E89.MirrorCS");var subQ1=sQuery(id+"F0.wireOp",EDGE,"E88.MirrorCS");var subQ2=makeQuery(id+"F0.imprint","INTERSECT",VERTEX,{"derivedFrom":[subQ1,subQ0]});Q30=makeQuery(id+"F0.imprint","IMPRINT",FACE,{"disambiguationData":[TD([[makeQuery(id+"F0.imprint","IMPRINT",EDGE,{"disambiguationData":[TD([[subQ2,1.0]])],"derivedFrom":subQ1}),-1.0]])]});}
            var Q31;
            {var subQ0=sQuery(id+"F0.wireOp",EDGE,"E123.MirrorCS");var subQ1=sQuery(id+"F0.wireOp",EDGE,"E88.MirrorCS");var subQ2=makeQuery(id+"F0.imprint","INTERSECT",VERTEX,{"derivedFrom":[subQ1,subQ0]});Q31=makeQuery(id+"F0.imprint","IMPRINT",FACE,{"disambiguationData":[TD([[makeQuery(id+"F0.imprint","IMPRINT",EDGE,{"disambiguationData":[TD([[subQ2,-1.0]])],"derivedFrom":subQ1}),-1.0]])]});}
            var Q32;
            {var subQ0=sQuery(id+"F0.wireOp",EDGE,"E124.MirrorCS");var subQ1=sQuery(id+"F0.wireOp",EDGE,"E90.MirrorCS");var subQ2=makeQuery(id+"F0.imprint","INTERSECT",VERTEX,{"derivedFrom":[subQ1,subQ0]});Q32=makeQuery(id+"F0.imprint","IMPRINT",FACE,{"disambiguationData":[TD([[makeQuery(id+"F0.imprint","IMPRINT",EDGE,{"disambiguationData":[TD([[subQ2,-1.0]])],"derivedFrom":subQ1}),1.0]])]});}
            var Q33;
            {var subQ0=sQuery(id+"F0.wireOp",EDGE,"E123.MirrorCS");var subQ1=sQuery(id+"F0.wireOp",EDGE,"E89.MirrorCS");var subQ2=makeQuery(id+"F0.imprint","INTERSECT",VERTEX,{"derivedFrom":[subQ1,subQ0]});Q33=makeQuery(id+"F0.imprint","IMPRINT",FACE,{"disambiguationData":[TD([[makeQuery(id+"F0.imprint","IMPRINT",EDGE,{"disambiguationData":[TD([[subQ2,1.0]])],"derivedFrom":subQ1}),-1.0]])]});}
            var Q34;
            {var subQ0=sQuery(id+"F0.wireOp",EDGE,"E124.MirrorCS");var subQ1=sQuery(id+"F0.wireOp",EDGE,"E92.MirrorCS");var subQ2=makeQuery(id+"F0.imprint","INTERSECT",VERTEX,{"derivedFrom":[subQ1,subQ0]});Q34=makeQuery(id+"F0.imprint","IMPRINT",FACE,{"disambiguationData":[TD([[makeQuery(id+"F0.imprint","IMPRINT",EDGE,{"disambiguationData":[TD([[subQ2,1.0]])],"derivedFrom":subQ1}),1.0]])]});}
            var Q35;
            {var subQ0=sQuery(id+"F0.wireOp",EDGE,"E92.MirrorCS");var subQ1=sQuery(id+"F0.wireOp",EDGE,"E90.MirrorCS");var subQ2=makeQuery(id+"F0.imprint","INTERSECT",VERTEX,{"derivedFrom":[subQ1,subQ0]});Q35=makeQuery(id+"F0.imprint","IMPRINT",FACE,{"disambiguationData":[TD([[makeQuery(id+"F0.imprint","IMPRINT",EDGE,{"disambiguationData":[TD([[subQ2,1.0]])],"derivedFrom":subQ1}),1.0]])]});}
            var Q36;
            {var subQ0=sQuery(id+"F0.wireOp",EDGE,"E93.MirrorCS");var subQ1=sQuery(id+"F0.wireOp",EDGE,"E87.MirrorCS");var subQ2=makeQuery(id+"F0.imprint","INTERSECT",VERTEX,{"derivedFrom":[subQ1,subQ0]});Q36=makeQuery(id+"F0.imprint","IMPRINT",FACE,{"disambiguationData":[TD([[makeQuery(id+"F0.imprint","IMPRINT",EDGE,{"disambiguationData":[TD([[subQ2,-1.0]])],"derivedFrom":subQ1}),1.0]])]});}
            var Q37;
            {var subQ0=sQuery(id+"F0.wireOp",EDGE,"E130.MirrorCS");var subQ1=sQuery(id+"F0.wireOp",EDGE,"E93.MirrorCS");var subQ2=makeQuery(id+"F0.imprint","INTERSECT",VERTEX,{"derivedFrom":[subQ1,subQ0]});Q37=makeQuery(id+"F0.imprint","IMPRINT",FACE,{"disambiguationData":[TD([[makeQuery(id+"F0.imprint","IMPRINT",EDGE,{"disambiguationData":[TD([[subQ2,1.0]])],"derivedFrom":subQ1}),-1.0]])]});}
            var Q38;
            {var subQ0=sQuery(id+"F0.wireOp",EDGE,"E131.MirrorCS");var subQ1=sQuery(id+"F0.wireOp",EDGE,"E91.MirrorCS");var subQ2=makeQuery(id+"F0.imprint","INTERSECT",VERTEX,{"derivedFrom":[subQ1,subQ0]});Q38=makeQuery(id+"F0.imprint","IMPRINT",FACE,{"disambiguationData":[TD([[makeQuery(id+"F0.imprint","IMPRINT",EDGE,{"disambiguationData":[TD([[subQ2,-1.0]])],"derivedFrom":subQ1}),-1.0]])]});}
            var Q39;
            {var subQ0=sQuery(id+"F0.wireOp",EDGE,"E130.MirrorCS");var subQ1=sQuery(id+"F0.wireOp",EDGE,"E87.MirrorCS");var subQ2=makeQuery(id+"F0.imprint","INTERSECT",VERTEX,{"derivedFrom":[subQ1,subQ0]});Q39=makeQuery(id+"F0.imprint","IMPRINT",FACE,{"disambiguationData":[TD([[makeQuery(id+"F0.imprint","IMPRINT",EDGE,{"disambiguationData":[TD([[subQ2,1.0]])],"derivedFrom":subQ1}),1.0]])]});}
            var Q40;
            {var subQ0=sQuery(id+"F0.wireOp",EDGE,"E131.MirrorCS");var subQ1=sQuery(id+"F0.wireOp",EDGE,"E94.MirrorCS");var subQ2=makeQuery(id+"F0.imprint","INTERSECT",VERTEX,{"derivedFrom":[subQ1,subQ0]});Q40=makeQuery(id+"F0.imprint","IMPRINT",FACE,{"disambiguationData":[TD([[makeQuery(id+"F0.imprint","IMPRINT",EDGE,{"disambiguationData":[TD([[subQ2,-1.0]])],"derivedFrom":subQ1}),1.0]])]});}
            var Q41;
            {var subQ0=sQuery(id+"F0.wireOp",EDGE,"E94.MirrorCS");var subQ1=sQuery(id+"F0.wireOp",EDGE,"E91.MirrorCS");var subQ2=makeQuery(id+"F0.imprint","INTERSECT",VERTEX,{"derivedFrom":[subQ1,subQ0]});Q41=makeQuery(id+"F0.imprint","IMPRINT",FACE,{"disambiguationData":[TD([[makeQuery(id+"F0.imprint","IMPRINT",EDGE,{"disambiguationData":[TD([[subQ2,1.0]])],"derivedFrom":subQ1}),-1.0]])]});}
            var Q42;
            {var subQ0=sQuery(id+"F0.wireOp",EDGE,"E134.MirrorCS");var subQ1=sQuery(id+"F0.wireOp",EDGE,"E108.MirrorCS");var subQ2=makeQuery(id+"F0.imprint","INTERSECT",VERTEX,{"derivedFrom":[subQ1,subQ0]});Q42=makeQuery(id+"F0.imprint","IMPRINT",FACE,{"disambiguationData":[TD([[makeQuery(id+"F0.imprint","IMPRINT",EDGE,{"disambiguationData":[TD([[subQ2,1.0]])],"derivedFrom":subQ1}),-1.0]])]});}
            var Q43;
            {var subQ0=sQuery(id+"F0.wireOp",EDGE,"E133.MirrorCS");var subQ1=sQuery(id+"F0.wireOp",EDGE,"E103.MirrorCS");var subQ2=makeQuery(id+"F0.imprint","INTERSECT",VERTEX,{"derivedFrom":[subQ1,subQ0]});Q43=makeQuery(id+"F0.imprint","IMPRINT",FACE,{"disambiguationData":[TD([[makeQuery(id+"F0.imprint","IMPRINT",EDGE,{"disambiguationData":[TD([[subQ2,-1.0]])],"derivedFrom":subQ1}),-1.0]])]});}
            var Q44;
            {var subQ0=sQuery(id+"F0.wireOp",EDGE,"E107.MirrorCS");var subQ1=sQuery(id+"F0.wireOp",EDGE,"E103.MirrorCS");var subQ2=makeQuery(id+"F0.imprint","INTERSECT",VERTEX,{"derivedFrom":[subQ1,subQ0]});Q44=makeQuery(id+"F0.imprint","IMPRINT",FACE,{"disambiguationData":[TD([[makeQuery(id+"F0.imprint","IMPRINT",EDGE,{"disambiguationData":[TD([[subQ2,1.0]])],"derivedFrom":subQ1}),-1.0]])]});}
            var Q45;
            {var subQ0=sQuery(id+"F0.wireOp",EDGE,"E108.MirrorCS");var subQ1=sQuery(id+"F0.wireOp",EDGE,"E105.MirrorCS");var subQ2=makeQuery(id+"F0.imprint","INTERSECT",VERTEX,{"derivedFrom":[subQ1,subQ0]});Q45=makeQuery(id+"F0.imprint","IMPRINT",FACE,{"disambiguationData":[TD([[makeQuery(id+"F0.imprint","IMPRINT",EDGE,{"disambiguationData":[TD([[subQ2,-1.0]])],"derivedFrom":subQ1}),1.0]])]});}
            var Q46;
            {var subQ0=sQuery(id+"F0.wireOp",EDGE,"E134.MirrorCS");var subQ1=sQuery(id+"F0.wireOp",EDGE,"E105.MirrorCS");var subQ2=makeQuery(id+"F0.imprint","INTERSECT",VERTEX,{"derivedFrom":[subQ1,subQ0]});Q46=makeQuery(id+"F0.imprint","IMPRINT",FACE,{"disambiguationData":[TD([[makeQuery(id+"F0.imprint","IMPRINT",EDGE,{"disambiguationData":[TD([[subQ2,1.0]])],"derivedFrom":subQ1}),1.0]])]});}
            var Q47;
            {var subQ0=sQuery(id+"F0.wireOp",EDGE,"E133.MirrorCS");var subQ1=sQuery(id+"F0.wireOp",EDGE,"E107.MirrorCS");var subQ2=makeQuery(id+"F0.imprint","INTERSECT",VERTEX,{"derivedFrom":[subQ1,subQ0]});Q47=makeQuery(id+"F0.imprint","IMPRINT",FACE,{"disambiguationData":[TD([[makeQuery(id+"F0.imprint","IMPRINT",EDGE,{"disambiguationData":[TD([[subQ2,-1.0]])],"derivedFrom":subQ1}),1.0]])]});}
            var Q48;
            {var subQ0=sQuery(id+"F0.wireOp",EDGE,"E127.MirrorCS");var subQ1=sQuery(id+"F0.wireOp",EDGE,"E110.MirrorCS");var subQ2=makeQuery(id+"F0.imprint","INTERSECT",VERTEX,{"derivedFrom":[subQ1,subQ0]});Q48=makeQuery(id+"F0.imprint","IMPRINT",FACE,{"disambiguationData":[TD([[makeQuery(id+"F0.imprint","IMPRINT",EDGE,{"disambiguationData":[TD([[subQ2,1.0]])],"derivedFrom":subQ1}),-1.0]])]});}
            var Q49;
            {var subQ0=sQuery(id+"F0.wireOp",EDGE,"E128.MirrorCS");var subQ1=sQuery(id+"F0.wireOp",EDGE,"E106.MirrorCS");var subQ2=makeQuery(id+"F0.imprint","INTERSECT",VERTEX,{"derivedFrom":[subQ1,subQ0]});Q49=makeQuery(id+"F0.imprint","IMPRINT",FACE,{"disambiguationData":[TD([[makeQuery(id+"F0.imprint","IMPRINT",EDGE,{"disambiguationData":[TD([[subQ2,1.0]])],"derivedFrom":subQ1}),1.0]])]});}
            var Q50;
            {var subQ0=sQuery(id+"F0.wireOp",EDGE,"E110.MirrorCS");var subQ1=sQuery(id+"F0.wireOp",EDGE,"E104.MirrorCS");var subQ2=makeQuery(id+"F0.imprint","INTERSECT",VERTEX,{"derivedFrom":[subQ1,subQ0]});Q50=makeQuery(id+"F0.imprint","IMPRINT",FACE,{"disambiguationData":[TD([[makeQuery(id+"F0.imprint","IMPRINT",EDGE,{"disambiguationData":[TD([[subQ2,1.0]])],"derivedFrom":subQ1}),-1.0]])]});}
            var Q51;
            {var subQ0=sQuery(id+"F0.wireOp",EDGE,"E127.MirrorCS");var subQ1=sQuery(id+"F0.wireOp",EDGE,"E104.MirrorCS");var subQ2=makeQuery(id+"F0.imprint","INTERSECT",VERTEX,{"derivedFrom":[subQ1,subQ0]});Q51=makeQuery(id+"F0.imprint","IMPRINT",FACE,{"disambiguationData":[TD([[makeQuery(id+"F0.imprint","IMPRINT",EDGE,{"disambiguationData":[TD([[subQ2,-1.0]])],"derivedFrom":subQ1}),-1.0]])]});}
            var Q52;
            {var subQ0=sQuery(id+"F0.wireOp",EDGE,"E128.MirrorCS");var subQ1=sQuery(id+"F0.wireOp",EDGE,"E109.MirrorCS");var subQ2=makeQuery(id+"F0.imprint","INTERSECT",VERTEX,{"derivedFrom":[subQ1,subQ0]});Q52=makeQuery(id+"F0.imprint","IMPRINT",FACE,{"disambiguationData":[TD([[makeQuery(id+"F0.imprint","IMPRINT",EDGE,{"disambiguationData":[TD([[subQ2,-1.0]])],"derivedFrom":subQ1}),1.0]])]});}
            var Q53;
            {var subQ0=sQuery(id+"F0.wireOp",EDGE,"E109.MirrorCS");var subQ1=sQuery(id+"F0.wireOp",EDGE,"E106.MirrorCS");var subQ2=makeQuery(id+"F0.imprint","INTERSECT",VERTEX,{"derivedFrom":[subQ1,subQ0]});Q53=makeQuery(id+"F0.imprint","IMPRINT",FACE,{"disambiguationData":[TD([[makeQuery(id+"F0.imprint","IMPRINT",EDGE,{"disambiguationData":[TD([[subQ2,-1.0]])],"derivedFrom":subQ1}),1.0]])]});}
            var Q54;
            {var subQ0=sQuery(id+"F0.wireOp",EDGE,"E119.MirrorCS");var subQ1=sQuery(id+"F0.wireOp",EDGE,"E96.MirrorCS");var subQ2=makeQuery(id+"F0.imprint","INTERSECT",VERTEX,{"derivedFrom":[subQ1,subQ0]});Q54=makeQuery(id+"F0.imprint","IMPRINT",FACE,{"disambiguationData":[TD([[makeQuery(id+"F0.imprint","IMPRINT",EDGE,{"disambiguationData":[TD([[subQ2,-1.0]])],"derivedFrom":subQ1}),1.0]])]});}
            var Q55;
            {var subQ0=sQuery(id+"F0.wireOp",EDGE,"E117.MirrorCS");var subQ1=sQuery(id+"F0.wireOp",EDGE,"E98.MirrorCS");var subQ2=makeQuery(id+"F0.imprint","INTERSECT",VERTEX,{"derivedFrom":[subQ1,subQ0]});Q55=makeQuery(id+"F0.imprint","IMPRINT",FACE,{"disambiguationData":[TD([[makeQuery(id+"F0.imprint","IMPRINT",EDGE,{"disambiguationData":[TD([[subQ2,-1.0]])],"derivedFrom":subQ1}),-1.0]])]});}
            var Q56;
            {var subQ0=sQuery(id+"F0.wireOp",EDGE,"E98.MirrorCS");var subQ1=sQuery(id+"F0.wireOp",EDGE,"E97.MirrorCS");var subQ2=makeQuery(id+"F0.imprint","INTERSECT",VERTEX,{"derivedFrom":[subQ1,subQ0]});Q56=makeQuery(id+"F0.imprint","IMPRINT",FACE,{"disambiguationData":[TD([[makeQuery(id+"F0.imprint","IMPRINT",EDGE,{"disambiguationData":[TD([[subQ2,-1.0]])],"derivedFrom":subQ1}),-1.0]])]});}
            var Q57;
            {var subQ0=sQuery(id+"F0.wireOp",EDGE,"E99.MirrorCS");var subQ1=sQuery(id+"F0.wireOp",EDGE,"E96.MirrorCS");var subQ2=makeQuery(id+"F0.imprint","INTERSECT",VERTEX,{"derivedFrom":[subQ1,subQ0]});Q57=makeQuery(id+"F0.imprint","IMPRINT",FACE,{"disambiguationData":[TD([[makeQuery(id+"F0.imprint","IMPRINT",EDGE,{"disambiguationData":[TD([[subQ2,1.0]])],"derivedFrom":subQ1}),1.0]])]});}
            var Q58;
            {var subQ0=sQuery(id+"F0.wireOp",EDGE,"E119.MirrorCS");var subQ1=sQuery(id+"F0.wireOp",EDGE,"E99.MirrorCS");var subQ2=makeQuery(id+"F0.imprint","INTERSECT",VERTEX,{"derivedFrom":[subQ1,subQ0]});Q58=makeQuery(id+"F0.imprint","IMPRINT",FACE,{"disambiguationData":[TD([[makeQuery(id+"F0.imprint","IMPRINT",EDGE,{"disambiguationData":[TD([[subQ2,1.0]])],"derivedFrom":subQ1}),1.0]])]});}
            var Q59;
            {var subQ0=sQuery(id+"F0.wireOp",EDGE,"E117.MirrorCS");var subQ1=sQuery(id+"F0.wireOp",EDGE,"E97.MirrorCS");var subQ2=makeQuery(id+"F0.imprint","INTERSECT",VERTEX,{"derivedFrom":[subQ1,subQ0]});Q59=makeQuery(id+"F0.imprint","IMPRINT",FACE,{"disambiguationData":[TD([[makeQuery(id+"F0.imprint","IMPRINT",EDGE,{"disambiguationData":[TD([[subQ2,1.0]])],"derivedFrom":subQ1}),-1.0]])]});}
            var Q60;
            {var subQ0=sQuery(id+"F0.wireOp",EDGE,"E101.MirrorCS");var subQ1=sQuery(id+"F0.wireOp",EDGE,"E95.MirrorCS");var subQ2=makeQuery(id+"F0.imprint","INTERSECT",VERTEX,{"derivedFrom":[subQ1,subQ0]});Q60=makeQuery(id+"F0.imprint","IMPRINT",FACE,{"disambiguationData":[TD([[makeQuery(id+"F0.imprint","IMPRINT",EDGE,{"disambiguationData":[TD([[subQ2,-1.0]])],"derivedFrom":subQ1}),1.0]])]});}
            var Q61;
            {var subQ0=sQuery(id+"F0.wireOp",EDGE,"E122.MirrorCS");var subQ1=sQuery(id+"F0.wireOp",EDGE,"E101.MirrorCS");var subQ2=makeQuery(id+"F0.imprint","INTERSECT",VERTEX,{"derivedFrom":[subQ1,subQ0]});Q61=makeQuery(id+"F0.imprint","IMPRINT",FACE,{"disambiguationData":[TD([[makeQuery(id+"F0.imprint","IMPRINT",EDGE,{"disambiguationData":[TD([[subQ2,1.0]])],"derivedFrom":subQ1}),-1.0]])]});}
            var Q62;
            {var subQ0=sQuery(id+"F0.wireOp",EDGE,"E120.MirrorCS");var subQ1=sQuery(id+"F0.wireOp",EDGE,"E100.MirrorCS");var subQ2=makeQuery(id+"F0.imprint","INTERSECT",VERTEX,{"derivedFrom":[subQ1,subQ0]});Q62=makeQuery(id+"F0.imprint","IMPRINT",FACE,{"disambiguationData":[TD([[makeQuery(id+"F0.imprint","IMPRINT",EDGE,{"disambiguationData":[TD([[subQ2,-1.0]])],"derivedFrom":subQ1}),-1.0]])]});}
            var Q63;
            {var subQ0=sQuery(id+"F0.wireOp",EDGE,"E122.MirrorCS");var subQ1=sQuery(id+"F0.wireOp",EDGE,"E95.MirrorCS");var subQ2=makeQuery(id+"F0.imprint","INTERSECT",VERTEX,{"derivedFrom":[subQ1,subQ0]});Q63=makeQuery(id+"F0.imprint","IMPRINT",FACE,{"disambiguationData":[TD([[makeQuery(id+"F0.imprint","IMPRINT",EDGE,{"disambiguationData":[TD([[subQ2,1.0]])],"derivedFrom":subQ1}),1.0]])]});}
            var Q64;
            {var subQ0=sQuery(id+"F0.wireOp",EDGE,"E120.MirrorCS");var subQ1=sQuery(id+"F0.wireOp",EDGE,"E102.MirrorCS");var subQ2=makeQuery(id+"F0.imprint","INTERSECT",VERTEX,{"derivedFrom":[subQ1,subQ0]});Q64=makeQuery(id+"F0.imprint","IMPRINT",FACE,{"disambiguationData":[TD([[makeQuery(id+"F0.imprint","IMPRINT",EDGE,{"disambiguationData":[TD([[subQ2,-1.0]])],"derivedFrom":subQ1}),1.0]])]});}
            var Q65;
            {var subQ0=sQuery(id+"F0.wireOp",EDGE,"E102.MirrorCS");var subQ1=sQuery(id+"F0.wireOp",EDGE,"E100.MirrorCS");var subQ2=makeQuery(id+"F0.imprint","INTERSECT",VERTEX,{"derivedFrom":[subQ1,subQ0]});Q65=makeQuery(id+"F0.imprint","IMPRINT",FACE,{"disambiguationData":[TD([[makeQuery(id+"F0.imprint","IMPRINT",EDGE,{"disambiguationData":[TD([[subQ2,1.0]])],"derivedFrom":subQ1}),-1.0]])]});}
            var Q66;
            {var subQ3=sQuery(id+"F0.wireOp",EDGE,"E171.MirrorC");var subQ6=sQuery(id+"F0.wireOp",EDGE,"E91.MirrorCS");var subQ14=makeQuery(id+"F0.imprint","INTERSECT",VERTEX,{"derivedFrom":[subQ6,subQ3]});Q66=makeQuery(id+"F0.imprint","IMPRINT",FACE,{"disambiguationData":[TD([[makeQuery(id+"F0.imprint","IMPRINT",EDGE,{"disambiguationData":[TD([[subQ14,-1.0]])],"derivedFrom":subQ6}),-1.0]])]});}
            var Q67;
            {var subQ0=sQuery(id+"F0.wireOp",EDGE,"E181.MirrorC");var subQ12=sQuery(id+"F0.wireOp",EDGE,"E103.MirrorCS");var subQ13=makeQuery(id+"F0.imprint","INTERSECT",VERTEX,{"derivedFrom":[subQ12,subQ0]});Q67=makeQuery(id+"F0.imprint","IMPRINT",FACE,{"disambiguationData":[TD([[makeQuery(id+"F0.imprint","IMPRINT",EDGE,{"disambiguationData":[TD([[subQ13,-1.0]])],"derivedFrom":subQ12}),-1.0]])]});}
            var Q68;
            {var subQ0=sQuery(id+"F0.wireOp",EDGE,"E180.MirrorC");var subQ1=makeQuery(id+"F0.imprint","INTERSECT",VERTEX,{"derivedFrom":[sQuery(id+"F0.wireOp",EDGE,"E107.MirrorCS"),subQ0]});Q68=makeQuery(id+"F0.imprint","IMPRINT",FACE,{"disambiguationData":[TD([[makeQuery(id+"F0.imprint","IMPRINT",EDGE,{"disambiguationData":[TD([[subQ1,-1.0]])],"derivedFrom":subQ0}),1.0]])]});}
            var Q69;
            {var subQ0=sQuery(id+"F0.wireOp",EDGE,"E181.MirrorC");var subQ1=makeQuery(id+"F0.imprint","INTERSECT",VERTEX,{"derivedFrom":[sQuery(id+"F0.wireOp",EDGE,"E103.MirrorCS"),subQ0]});Q69=makeQuery(id+"F0.imprint","IMPRINT",FACE,{"disambiguationData":[TD([[makeQuery(id+"F0.imprint","IMPRINT",EDGE,{"disambiguationData":[TD([[subQ1,-1.0]])],"derivedFrom":subQ0}),1.0]])]});}
            var Q70;
            {var subQ0=sQuery(id+"F0.wireOp",EDGE,"E182.MirrorC");var subQ1=makeQuery(id+"F0.imprint","INTERSECT",VERTEX,{"derivedFrom":[sQuery(id+"F0.wireOp",EDGE,"E103.MirrorCS"),subQ0]});Q70=makeQuery(id+"F0.imprint","IMPRINT",FACE,{"disambiguationData":[TD([[makeQuery(id+"F0.imprint","IMPRINT",EDGE,{"disambiguationData":[TD([[subQ1,1.0]])],"derivedFrom":subQ0}),1.0]])]});}
            var Q71;
            {var subQ0=sQuery(id+"F0.wireOp",EDGE,"E175.MirrorC");var subQ1=makeQuery(id+"F0.imprint","INTERSECT",VERTEX,{"derivedFrom":[sQuery(id+"F0.wireOp",EDGE,"E94.MirrorCS"),subQ0]});Q71=makeQuery(id+"F0.imprint","IMPRINT",FACE,{"disambiguationData":[TD([[makeQuery(id+"F0.imprint","IMPRINT",EDGE,{"disambiguationData":[TD([[subQ1,-1.0]])],"derivedFrom":subQ0}),-1.0]])]});}
            var Q72;
            {var subQ0=sQuery(id+"F0.wireOp",EDGE,"E176.MirrorC");var subQ1=makeQuery(id+"F0.imprint","INTERSECT",VERTEX,{"derivedFrom":[sQuery(id+"F0.wireOp",EDGE,"E91.MirrorCS"),subQ0]});Q72=makeQuery(id+"F0.imprint","IMPRINT",FACE,{"disambiguationData":[TD([[makeQuery(id+"F0.imprint","IMPRINT",EDGE,{"disambiguationData":[TD([[subQ1,-1.0]])],"derivedFrom":subQ0}),-1.0]])]});}
            var Q73;
            {var subQ0=sQuery(id+"F0.wireOp",EDGE,"E171.MirrorC");var subQ1=makeQuery(id+"F0.imprint","INTERSECT",VERTEX,{"derivedFrom":[sQuery(id+"F0.wireOp",EDGE,"E91.MirrorCS"),subQ0]});Q73=makeQuery(id+"F0.imprint","IMPRINT",FACE,{"disambiguationData":[TD([[makeQuery(id+"F0.imprint","IMPRINT",EDGE,{"disambiguationData":[TD([[subQ1,-1.0]])],"derivedFrom":subQ0}),-1.0]])]});}
            var Q74;
            {var subQ1=sQuery(id+"F0.wireOp",EDGE,"E86.top");var subQ8=sQuery(id+"F0.wireOp",EDGE,"E137");var subQ11=makeQuery(id+"F0.imprint","INTERSECT",VERTEX,{"derivedFrom":[subQ1,subQ8]});Q74=makeQuery(id+"F0.imprint","IMPRINT",FACE,{"disambiguationData":[TD([[makeQuery(id+"F0.imprint","IMPRINT",EDGE,{"disambiguationData":[TD([[subQ11,-1.0]])],"derivedFrom":subQ1}),1.0]])]});}
            var Q75;
            {var subQ3=sQuery(id+"F0.wireOp",EDGE,"E150.MirrorC");var subQ6=sQuery(id+"F0.wireOp",EDGE,"E100.MirrorCS");var subQ11=makeQuery(id+"F0.imprint","INTERSECT",VERTEX,{"derivedFrom":[subQ6,subQ3]});Q75=makeQuery(id+"F0.imprint","IMPRINT",FACE,{"disambiguationData":[TD([[makeQuery(id+"F0.imprint","IMPRINT",EDGE,{"disambiguationData":[TD([[subQ11,-1.0]])],"derivedFrom":subQ6}),-1.0]])]});}
            var Q76;
            {var subQ0=sQuery(id+"F0.wireOp",EDGE,"E137");var subQ1=makeQuery(id+"F0.imprint","INTERSECT",VERTEX,{"derivedFrom":[sQuery(id+"F0.wireOp",EDGE,"E86.top"),subQ0]});Q76=makeQuery(id+"F0.imprint","IMPRINT",FACE,{"disambiguationData":[TD([[makeQuery(id+"F0.imprint","IMPRINT",EDGE,{"disambiguationData":[TD([[subQ1,-1.0]])],"derivedFrom":subQ0}),1.0]])]});}
            var Q77;
            {var subQ0=sQuery(id+"F0.wireOp",EDGE,"E135");var subQ1=makeQuery(id+"F0.imprint","INTERSECT",VERTEX,{"derivedFrom":[sQuery(id+"F0.wireOp",EDGE,"E86.top"),subQ0]});Q77=makeQuery(id+"F0.imprint","IMPRINT",FACE,{"disambiguationData":[TD([[makeQuery(id+"F0.imprint","IMPRINT",EDGE,{"disambiguationData":[TD([[subQ1,-1.0]])],"derivedFrom":subQ0}),1.0]])]});}
            var Q78;
            {var subQ0=sQuery(id+"F0.wireOp",EDGE,"E148.MirrorC");var subQ1=makeQuery(id+"F0.imprint","INTERSECT",VERTEX,{"derivedFrom":[sQuery(id+"F0.wireOp",EDGE,"E102.MirrorCS"),subQ0]});Q78=makeQuery(id+"F0.imprint","IMPRINT",FACE,{"disambiguationData":[TD([[makeQuery(id+"F0.imprint","IMPRINT",EDGE,{"disambiguationData":[TD([[subQ1,-1.0]])],"derivedFrom":subQ0}),-1.0]])]});}
            var Q79;
            {var subQ0=sQuery(id+"F0.wireOp",EDGE,"E147.MirrorC");var subQ1=makeQuery(id+"F0.imprint","INTERSECT",VERTEX,{"derivedFrom":[sQuery(id+"F0.wireOp",EDGE,"E100.MirrorCS"),subQ0]});Q79=makeQuery(id+"F0.imprint","IMPRINT",FACE,{"disambiguationData":[TD([[makeQuery(id+"F0.imprint","IMPRINT",EDGE,{"disambiguationData":[TD([[subQ1,-1.0]])],"derivedFrom":subQ0}),-1.0]])]});}
            var Q80;
            {var subQ0=sQuery(id+"F0.wireOp",EDGE,"E150.MirrorC");var subQ1=makeQuery(id+"F0.imprint","INTERSECT",VERTEX,{"derivedFrom":[sQuery(id+"F0.wireOp",EDGE,"E100.MirrorCS"),subQ0]});Q80=makeQuery(id+"F0.imprint","IMPRINT",FACE,{"disambiguationData":[TD([[makeQuery(id+"F0.imprint","IMPRINT",EDGE,{"disambiguationData":[TD([[subQ1,-1.0]])],"derivedFrom":subQ0}),-1.0]])]});}
            var Q81;
            {var subQ0=sQuery(id+"F0.wireOp",EDGE,"E136");var subQ1=makeQuery(id+"F0.imprint","INTERSECT",VERTEX,{"derivedFrom":[sQuery(id+"F0.wireOp",EDGE,"E86.right"),subQ0]});Q81=makeQuery(id+"F0.imprint","IMPRINT",FACE,{"disambiguationData":[TD([[makeQuery(id+"F0.imprint","IMPRINT",EDGE,{"disambiguationData":[TD([[subQ1,-1.0]])],"derivedFrom":subQ0}),1.0]])]});}
            var Q82;
            {var subQ48=sQuery(id+"F0.wireOp",EDGE,"E28.MirrorC");Q82=makeQuery(id+"F0.imprint","IMPRINT",FACE,{"disambiguationData":[TD([[makeQuery(id+"F0.imprint","IMPRINT",EDGE,{"derivedFrom":subQ48}),1.0]])]});}
            var Q83;
            {var subQ68=sQuery(id+"F0.wireOp",EDGE,"E27.MirrorC");Q83=makeQuery(id+"F0.imprint","IMPRINT",FACE,{"disambiguationData":[TD([[makeQuery(id+"F0.imprint","IMPRINT",EDGE,{"derivedFrom":subQ68}),1.0]])]});}
            var Q84;
            Q84=makeQuery(id+"F0.imprint","IMPRINT",FACE,{"disambiguationData":[TD([[makeQuery(id+"F0.imprint","IMPRINT",EDGE,{"derivedFrom":sQuery(id+"F0.wireOp",EDGE,"E65.MirrorCS")}),1.0]])]});
            var Q85;
            {var subQ1=sQuery(id+"F0.wireOp",EDGE,"E8");Q85=makeQuery(id+"F0.imprint","IMPRINT",FACE,{"disambiguationData":[TD([[makeQuery(id+"F0.imprint","IMPRINT",EDGE,{"derivedFrom":subQ1}),-1.0]])]});}
            var Q86;
            {var subQ9=sQuery(id+"F0.wireOp",EDGE,"E42.MirrorCS");Q86=makeQuery(id+"F0.imprint","IMPRINT",FACE,{"disambiguationData":[TD([[makeQuery(id+"F0.imprint","IMPRINT",EDGE,{"derivedFrom":subQ9}),1.0]])]});}
            var Q87;
            Q87=makeQuery(id+"F0.imprint","IMPRINT",FACE,{"disambiguationData":[TD([[makeQuery(id+"F0.imprint","IMPRINT",EDGE,{"derivedFrom":sQuery(id+"F0.wireOp",EDGE,"E53")}),-1.0]])]});
            var Q88;
            Q88=makeQuery(id+"F0.imprint","IMPRINT",FACE,{"disambiguationData":[TD([[makeQuery(id+"F0.imprint","IMPRINT",EDGE,{"derivedFrom":sQuery(id+"F0.wireOp",EDGE,"E57.MirrorCS")}),1.0]])]});
            var Q89;
            {var subQ11=sQuery(id+"F0.wireOp",EDGE,"E41.MirrorCS");Q89=makeQuery(id+"F0.imprint","IMPRINT",FACE,{"disambiguationData":[TD([[makeQuery(id+"F0.imprint","IMPRINT",EDGE,{"derivedFrom":subQ11}),1.0]])]});}
            var Q90;
            Q90=makeQuery(id+"F0.imprint","IMPRINT",FACE,{"disambiguationData":[TD([[makeQuery(id+"F0.imprint","IMPRINT",EDGE,{"derivedFrom":sQuery(id+"F0.wireOp",EDGE,"E61.MirrorCS")}),-1.0]])]});
            var Q91;
            {var subQ5=sQuery(id+"F0.wireOp",EDGE,"E13");Q91=makeQuery(id+"F0.imprint","IMPRINT",FACE,{"disambiguationData":[TD([[makeQuery(id+"F0.imprint","IMPRINT",EDGE,{"derivedFrom":subQ5}),-1.0]])]});}
            var Q92;
            {var subQ0=sQuery(id+"F0.wireOp",EDGE,"a028415d-a872-4f5b-9a31-fa1da7ace0e80.MirrorCS");Q92=makeQuery(id+"F0.imprint","IMPRINT",FACE,{"disambiguationData":[TD([[makeQuery(id+"F0.imprint","IMPRINT",EDGE,{"derivedFrom":subQ0}),-1.0]])]});}
            var Q93;
            {var subQ1=sQuery(id+"F0.wireOp",EDGE,"e31bf78d-551e-4e86-82ef-f6507e040a1d");Q93=makeQuery(id+"F0.imprint","IMPRINT",FACE,{"disambiguationData":[TD([[makeQuery(id+"F0.imprint","IMPRINT",EDGE,{"derivedFrom":subQ1}),1.0]])]});}
            var Q94;
            {var subQ3=sQuery(id+"F0.wireOp",EDGE,"E209");var subQ6=sQuery(id+"F0.wireOp",EDGE,"E10");var subQ9=makeQuery(id+"F0.imprint","INTERSECT",VERTEX,{"disambiguationData":[OD(1.0)],"derivedFrom":[subQ6,subQ3]});Q94=makeQuery(id+"F0.imprint","IMPRINT",FACE,{"disambiguationData":[TD([[makeQuery(id+"F0.imprint","IMPRINT",EDGE,{"disambiguationData":[TD([[subQ9,-1.0]])],"derivedFrom":subQ6}),-1.0]])]});}
            var Q95;
            {var subQ0=sQuery(id+"F0.wireOp",EDGE,"E209");var subQ1=sQuery(id+"F0.wireOp",EDGE,"E10");var subQ2=makeQuery(id+"F0.imprint","INTERSECT",VERTEX,{"disambiguationData":[OD(0.0)],"derivedFrom":[subQ1,subQ0]});Q95=makeQuery(id+"F0.imprint","IMPRINT",FACE,{"disambiguationData":[TD([[makeQuery(id+"F0.imprint","IMPRINT",EDGE,{"disambiguationData":[TD([[subQ2,-1.0]])],"derivedFrom":subQ1}),-1.0]])]});}
            var Q96;
            {var subQ0=sQuery(id+"F0.wireOp",EDGE,"E209");var subQ1=sQuery(id+"F0.wireOp",EDGE,"E5");var subQ2=makeQuery(id+"F0.imprint","INTERSECT",VERTEX,{"disambiguationData":[OD(0.0)],"derivedFrom":[subQ1,subQ0]});Q96=makeQuery(id+"F0.imprint","IMPRINT",FACE,{"disambiguationData":[TD([[makeQuery(id+"F0.imprint","IMPRINT",EDGE,{"disambiguationData":[TD([[subQ2,-1.0]])],"derivedFrom":subQ1}),1.0]])]});}
            var Q97;
            {var subQ0=sQuery(id+"F0.wireOp",EDGE,"E209");var subQ1=sQuery(id+"F0.wireOp",EDGE,"E5");var subQ2=makeQuery(id+"F0.imprint","INTERSECT",VERTEX,{"disambiguationData":[OD(0.0)],"derivedFrom":[subQ1,subQ0]});Q97=makeQuery(id+"F0.imprint","IMPRINT",FACE,{"disambiguationData":[TD([[makeQuery(id+"F0.imprint","IMPRINT",EDGE,{"disambiguationData":[TD([[subQ2,-1.0]])],"derivedFrom":subQ1}),-1.0]])]});}
            var Q98;
            {var subQ3=sQuery(id+"F0.wireOp",EDGE,"E212");var subQ6=sQuery(id+"F0.wireOp",EDGE,"E16");var subQ11=makeQuery(id+"F0.imprint","INTERSECT",VERTEX,{"disambiguationData":[OD(1.0)],"derivedFrom":[subQ6,subQ3]});Q98=makeQuery(id+"F0.imprint","IMPRINT",FACE,{"disambiguationData":[TD([[makeQuery(id+"F0.imprint","IMPRINT",EDGE,{"disambiguationData":[TD([[subQ11,-1.0]])],"derivedFrom":subQ6}),1.0]])]});}
            var Q99;
            {var subQ0=sQuery(id+"F0.wireOp",EDGE,"E213");var subQ1=sQuery(id+"F0.wireOp",EDGE,"E33.MirrorCS");var subQ2=makeQuery(id+"F0.imprint","INTERSECT",VERTEX,{"disambiguationData":[OD(0.0)],"derivedFrom":[subQ1,subQ0]});Q99=makeQuery(id+"F0.imprint","IMPRINT",FACE,{"disambiguationData":[TD([[makeQuery(id+"F0.imprint","IMPRINT",EDGE,{"disambiguationData":[TD([[subQ2,-1.0]])],"derivedFrom":subQ1}),-1.0]])]});}
            var Q100;
            {var subQ0=sQuery(id+"F0.wireOp",EDGE,"E213");var subQ2=sQuery(id+"F0.wireOp",EDGE,"E30.MirrorC");var subQ4=makeQuery(id+"F0.imprint","INTERSECT",VERTEX,{"disambiguationData":[OD(0.0)],"derivedFrom":[subQ2,subQ0]});Q100=makeQuery(id+"F0.imprint","IMPRINT",FACE,{"disambiguationData":[TD([[makeQuery(id+"F0.imprint","IMPRINT",EDGE,{"disambiguationData":[TD([[subQ4,-1.0]])],"derivedFrom":subQ2}),1.0]])]});}
            var Q101;
            {var subQ0=sQuery(id+"F0.wireOp",EDGE,"E213");var subQ1=sQuery(id+"F0.wireOp",EDGE,"E43.MirrorCS");var subQ2=makeQuery(id+"F0.imprint","INTERSECT",VERTEX,{"disambiguationData":[OD(0.0)],"derivedFrom":[subQ1,subQ0]});Q101=makeQuery(id+"F0.imprint","IMPRINT",FACE,{"disambiguationData":[TD([[makeQuery(id+"F0.imprint","IMPRINT",EDGE,{"disambiguationData":[TD([[subQ2,-1.0]])],"derivedFrom":subQ1}),-1.0]])]});}
            var Q102;
            {var subQ0=sQuery(id+"F0.wireOp",EDGE,"E34.MirrorCS");var subQ3=sQuery(id+"F0.wireOp",EDGE,"E213");var subQ5=makeQuery(id+"F0.imprint","INTERSECT",VERTEX,{"derivedFrom":[subQ0,subQ3]});Q102=makeQuery(id+"F0.imprint","IMPRINT",FACE,{"disambiguationData":[TD([[makeQuery(id+"F0.imprint","IMPRINT",EDGE,{"disambiguationData":[TD([[subQ5,-1.0]])],"derivedFrom":subQ3}),-1.0]])]});}
            var Q103;
            {var subQ0=sQuery(id+"F0.wireOp",EDGE,"E212");var subQ1=sQuery(id+"F0.wireOp",EDGE,"E16");var subQ2=makeQuery(id+"F0.imprint","INTERSECT",VERTEX,{"disambiguationData":[OD(0.0)],"derivedFrom":[subQ1,subQ0]});Q103=makeQuery(id+"F0.imprint","IMPRINT",FACE,{"disambiguationData":[TD([[makeQuery(id+"F0.imprint","IMPRINT",EDGE,{"disambiguationData":[TD([[subQ2,-1.0]])],"derivedFrom":subQ1}),1.0]])]});}
            var Q104;
            {var subQ0=sQuery(id+"F0.wireOp",EDGE,"E212");var subQ1=sQuery(id+"F0.wireOp",EDGE,"E12");var subQ2=makeQuery(id+"F0.imprint","INTERSECT",VERTEX,{"disambiguationData":[OD(0.0)],"derivedFrom":[subQ1,subQ0]});Q104=makeQuery(id+"F0.imprint","IMPRINT",FACE,{"disambiguationData":[TD([[makeQuery(id+"F0.imprint","IMPRINT",EDGE,{"disambiguationData":[TD([[subQ2,-1.0]])],"derivedFrom":subQ1}),1.0]])]});}
            var Q105;
            {var subQ0=sQuery(id+"F0.wireOp",EDGE,"E212");var subQ2=sQuery(id+"F0.wireOp",EDGE,"E4");var subQ3=makeQuery(id+"F0.imprint","INTERSECT",VERTEX,{"disambiguationData":[OD(0.0)],"derivedFrom":[subQ2,subQ0]});Q105=makeQuery(id+"F0.imprint","IMPRINT",FACE,{"disambiguationData":[TD([[makeQuery(id+"F0.imprint","IMPRINT",EDGE,{"disambiguationData":[TD([[subQ3,1.0]])],"derivedFrom":subQ2}),-1.0]])]});}
            var Q106;
            {var subQ0=sQuery(id+"F0.wireOp",EDGE,"E210");var subQ5=sQuery(id+"F0.wireOp",EDGE,"E26.MirrorC");var subQ6=makeQuery(id+"F0.imprint","INTERSECT",VERTEX,{"disambiguationData":[OD(0.0)],"derivedFrom":[subQ5,subQ0]});Q106=makeQuery(id+"F0.imprint","IMPRINT",FACE,{"disambiguationData":[TD([[makeQuery(id+"F0.imprint","IMPRINT",EDGE,{"disambiguationData":[TD([[subQ6,1.0]])],"derivedFrom":subQ5}),1.0]])]});}
            var Q107;
            {var subQ0=sQuery(id+"F0.wireOp",EDGE,"E210");var subQ1=sQuery(id+"F0.wireOp",EDGE,"E35.MirrorCS");var subQ2=makeQuery(id+"F0.imprint","INTERSECT",VERTEX,{"disambiguationData":[OD(0.0)],"derivedFrom":[subQ1,subQ0]});Q107=makeQuery(id+"F0.imprint","IMPRINT",FACE,{"disambiguationData":[TD([[makeQuery(id+"F0.imprint","IMPRINT",EDGE,{"disambiguationData":[TD([[subQ2,-1.0]])],"derivedFrom":subQ1}),-1.0]])]});}
            var Q108;
            {var subQ0=sQuery(id+"F0.wireOp",EDGE,"E210");var subQ1=sQuery(id+"F0.wireOp",EDGE,"E35.MirrorCS");var subQ2=makeQuery(id+"F0.imprint","INTERSECT",VERTEX,{"disambiguationData":[OD(0.0)],"derivedFrom":[subQ1,subQ0]});Q108=makeQuery(id+"F0.imprint","IMPRINT",FACE,{"disambiguationData":[TD([[makeQuery(id+"F0.imprint","IMPRINT",EDGE,{"disambiguationData":[TD([[subQ2,-1.0]])],"derivedFrom":subQ1}),1.0]])]});}
            extrude(context, id + "F1", {"entities" : qUnion([Q0, Q1, Q2, Q3, Q4, Q5, Q6, Q7, Q8, Q9, Q10, Q11, Q12, Q13, Q14, Q15, Q16, Q17, Q18, Q19, Q20, Q21, Q22, Q23, Q24, Q25, Q26, Q27, Q28, Q29, Q30, Q31, Q32, Q33, Q34, Q35, Q36, Q37, Q38, Q39, Q40, Q41, Q42, Q43, Q44, Q45, Q46, Q47, Q48, Q49, Q50, Q51, Q52, Q53, Q54, Q55, Q56, Q57, Q58, Q59, Q60, Q61, Q62, Q63, Q64, Q65, Q66, Q67, Q68, Q69, Q70, Q71, Q72, Q73, Q74, Q75, Q76, Q77, Q78, Q79, Q80, Q81, Q82, Q83, Q84, Q85, Q86, Q87, Q88, Q89, Q90, Q91, Q92, Q93, Q94, Q95, Q96, Q97, Q98, Q99, Q100, Q101, Q102, Q103, Q104, Q105, Q106, Q107, Q108]), "depth" : 1.5 * mm});
        }
        {
            var Q0;
            Q0=qCreatedBy(makeId("Top.planeOp"),FACE);
            var sketch = newSketch(context, id + "F2", { "sketchPlane" : qUnion([Q0])});
            skLineSegment(sketch, "E214.bottom", {"start": v(139.97, 590.64) * mm, "end": v(-113.53, 590.64) * mm});
            skLineSegment(sketch, "E214.top", {"start": v(139.97, 540.64) * mm, "end": v(-113.53, 540.64) * mm});
            skLineSegment(sketch, "E214.left", {"start": v(149.97, 580.64) * mm, "end": v(149.97, 550.64) * mm});
            skLineSegment(sketch, "E214.right", {"start": v(-129.03, 587.64) * mm, "end": v(-129.03, 543.64) * mm});
            skCircle(sketch, "E215", {"center": v(-38.28, 585.64) * mm, "radius": 1.5 * mm});
            skCircle(sketch, "E216", {"center": v(-63.28, 585.64) * mm, "radius": 1.5 * mm});
            skCircle(sketch, "E217", {"center": v(15.97, 585.64) * mm, "radius": 1.5 * mm});
            skCircle(sketch, "E218", {"center": v(50.97, 585.64) * mm, "radius": 1.5 * mm});
            skLineSegment(sketch, "E219", {"start": v(149.97, 565.64) * mm, "end": v(-129.03, 565.64) * mm});
            skCircle(sketch, "E220", {"center": v(-102.03, 585.64) * mm, "radius": 1.5 * mm});
            skCircle(sketch, "E221", {"center": v(133.97, 585.64) * mm, "radius": 1.5 * mm});
            skCircle(sketch, "E222.MirrorC", {"center": v(133.97, 545.64) * mm, "radius": 1.5 * mm});
            skCircle(sketch, "E223.MirrorC", {"center": v(50.97, 545.64) * mm, "radius": 1.5 * mm});
            skCircle(sketch, "E224.MirrorC", {"center": v(-38.28, 545.64) * mm, "radius": 1.5 * mm});
            skCircle(sketch, "E225.MirrorC", {"center": v(-102.03, 545.64) * mm, "radius": 1.5 * mm});
            skCircle(sketch, "E226.MirrorC", {"center": v(15.97, 545.64) * mm, "radius": 1.5 * mm});
            skCircle(sketch, "E227.MirrorC", {"center": v(-63.28, 545.64) * mm, "radius": 1.5 * mm});
            skLineSegment(sketch, "E228.bottom", {"start": v(0.72, 580.9) * mm, "end": v(31.22, 580.9) * mm});
            skLineSegment(sketch, "E228.top", {"start": v(0.72, 550.4) * mm, "end": v(31.22, 550.4) * mm});
            skLineSegment(sketch, "E228.left", {"start": v(0.72, 580.9) * mm, "end": v(0.72, 550.4) * mm});
            skLineSegment(sketch, "E228.right", {"start": v(31.22, 580.9) * mm, "end": v(31.22, 550.4) * mm});
            skPoint(sketch, "E229", {"position": v(31.22, 565.64) * mm});
            skPoint(sketch, "E230", {"position": v(15.97, 580.9) * mm});
            skCircle(sketch, "E231", {"center": v(0.72, 580.9) * mm, "radius": 1.5 * mm});
            skCircle(sketch, "E232", {"center": v(31.22, 580.9) * mm, "radius": 1.5 * mm});
            skCircle(sketch, "E233", {"center": v(31.22, 550.4) * mm, "radius": 1.5 * mm});
            skCircle(sketch, "E234", {"center": v(0.72, 550.4) * mm, "radius": 1.5 * mm});
            skLineSegment(sketch, "E235.bottom", {"start": v(50.22, 580.64) * mm, "end": v(90.22, 580.64) * mm});
            skLineSegment(sketch, "E235.top", {"start": v(48.22, 550.64) * mm, "end": v(86.22, 550.64) * mm});
            skLineSegment(sketch, "E235.left", {"start": v(48.22, 578.64) * mm, "end": v(48.22, 550.64) * mm});
            skLineSegment(sketch, "E235.right", {"start": v(90.22, 580.64) * mm, "end": v(90.22, 554.64) * mm});
            skLineSegment(sketch, "E236.bottom", {"start": v(100.22, 580.64) * mm, "end": v(140.22, 580.64) * mm});
            skLineSegment(sketch, "E236.top", {"start": v(104.22, 550.64) * mm, "end": v(142.22, 550.64) * mm});
            skLineSegment(sketch, "E236.left", {"start": v(100.22, 580.64) * mm, "end": v(100.22, 554.64) * mm});
            skLineSegment(sketch, "E236.right", {"start": v(142.22, 578.64) * mm, "end": v(142.22, 550.64) * mm});
            skLineSegment(sketch, "E237.bottom", {"start": v(-14.28, 580.64) * mm, "end": v(-54.28, 580.64) * mm});
            skLineSegment(sketch, "E237.top", {"start": v(-16.28, 550.64) * mm, "end": v(-56.28, 550.64) * mm});
            skLineSegment(sketch, "E237.left", {"start": v(-14.28, 580.64) * mm, "end": v(-14.28, 552.64) * mm});
            skLineSegment(sketch, "E237.right", {"start": v(-56.28, 578.64) * mm, "end": v(-56.28, 550.64) * mm});
            skLineSegment(sketch, "E238.bottom", {"start": v(-68.28, 580.64) * mm, "end": v(-108.28, 580.64) * mm});
            skLineSegment(sketch, "E238.top", {"start": v(-66.28, 550.64) * mm, "end": v(-106.28, 550.64) * mm});
            skLineSegment(sketch, "E238.left", {"start": v(-66.28, 578.64) * mm, "end": v(-66.28, 550.64) * mm});
            skLineSegment(sketch, "E238.right", {"start": v(-108.28, 580.64) * mm, "end": v(-108.28, 552.64) * mm});
            skCircle(sketch, "E239", {"center": v(-122.03, 585.64) * mm, "radius": 1.5 * mm});
            skCircle(sketch, "E240.MirrorC", {"center": v(-122.03, 545.64) * mm, "radius": 1.5 * mm});
            skLineSegment(sketch, "E241.bottom", {"start": v(4.72, 576.9) * mm, "end": v(27.22, 576.9) * mm});
            skLineSegment(sketch, "E241.top", {"start": v(4.72, 554.4) * mm, "end": v(27.22, 554.4) * mm});
            skLineSegment(sketch, "E241.left", {"start": v(4.72, 576.9) * mm, "end": v(4.72, 554.4) * mm});
            skLineSegment(sketch, "E241.right", {"start": v(27.22, 576.9) * mm, "end": v(27.22, 554.4) * mm});
            skLineSegment(sketch, "E242", {"start": v(4.72, 576.9) * mm, "end": v(27.22, 554.4) * mm});
            skLineSegment(sketch, "E243", {"start": v(6.84, 576.9) * mm, "end": v(27.22, 556.51) * mm});
            skLineSegment(sketch, "E244", {"start": v(4.72, 574.77) * mm, "end": v(25.1, 554.4) * mm});
            skLineSegment(sketch, "E245", {"start": v(4.72, 554.4) * mm, "end": v(27.22, 576.9) * mm});
            skLineSegment(sketch, "E246", {"start": v(4.72, 556.51) * mm, "end": v(25.1, 576.9) * mm});
            skLineSegment(sketch, "E247", {"start": v(6.84, 554.4) * mm, "end": v(27.22, 574.77) * mm});
            skCircle(sketch, "E248", {"center": v(9.25, 575.9) * mm, "radius": 1 * mm});
            skCircle(sketch, "E249", {"center": v(15.97, 569.18) * mm, "radius": 1 * mm});
            skCircle(sketch, "E250", {"center": v(22.68, 575.9) * mm, "radius": 1 * mm});
            skCircle(sketch, "E251", {"center": v(26.22, 572.36) * mm, "radius": 1 * mm});
            skCircle(sketch, "E252", {"center": v(19.5, 565.64) * mm, "radius": 1 * mm});
            skCircle(sketch, "E253", {"center": v(5.72, 572.36) * mm, "radius": 1 * mm});
            skCircle(sketch, "E254", {"center": v(12.43, 565.64) * mm, "radius": 1 * mm});
            skCircle(sketch, "E255.MirrorC", {"center": v(5.72, 558.93) * mm, "radius": 1 * mm});
            skCircle(sketch, "E256.MirrorC", {"center": v(9.25, 555.4) * mm, "radius": 1 * mm});
            skCircle(sketch, "E257.MirrorC", {"center": v(15.97, 562.1) * mm, "radius": 1 * mm});
            skCircle(sketch, "E258.MirrorC", {"center": v(22.68, 555.4) * mm, "radius": 1 * mm});
            skCircle(sketch, "E259.MirrorC", {"center": v(26.22, 558.93) * mm, "radius": 1 * mm});
            skPoint(sketch, "E260.visualSharp", {"position": v(149.97, 590.64) * mm});
            skArc(sketch, "E260.filletArc", {"start": v(149.97, 580.64) * mm, "mid": v(147.04, 587.71) * mm, "end": v(139.97, 590.64) * mm});
            skPoint(sketch, "E261.visualSharp", {"position": v(149.97, 540.64) * mm});
            skArc(sketch, "E261.filletArc", {"start": v(139.97, 540.64) * mm, "mid": v(147.04, 543.57) * mm, "end": v(149.97, 550.64) * mm});
            skLineSegment(sketch, "E262", {"start": v(-108.28, 580.64) * mm, "end": v(-66.28, 550.64) * mm});
            skLineSegment(sketch, "E263", {"start": v(-103.98, 580.64) * mm, "end": v(-66.28, 553.71) * mm});
            skLineSegment(sketch, "E264", {"start": v(-108.28, 577.57) * mm, "end": v(-70.58, 550.64) * mm});
            skLineSegment(sketch, "E265", {"start": v(-56.28, 550.64) * mm, "end": v(-14.28, 580.64) * mm});
            skLineSegment(sketch, "E266", {"start": v(-56.28, 553.71) * mm, "end": v(-18.58, 580.64) * mm});
            skLineSegment(sketch, "E267", {"start": v(-51.98, 550.64) * mm, "end": v(-14.28, 577.57) * mm});
            skLineSegment(sketch, "E268", {"start": v(48.22, 550.64) * mm, "end": v(90.22, 580.64) * mm});
            skLineSegment(sketch, "E269", {"start": v(48.22, 553.71) * mm, "end": v(85.92, 580.64) * mm});
            skLineSegment(sketch, "E270", {"start": v(90.22, 577.57) * mm, "end": v(52.52, 550.64) * mm});
            skLineSegment(sketch, "E271", {"start": v(100.22, 580.64) * mm, "end": v(139.97, 550.64) * mm});
            skLineSegment(sketch, "E272", {"start": v(104.37, 580.64) * mm, "end": v(142.22, 552.08) * mm});
            skLineSegment(sketch, "E273", {"start": v(100.22, 577.5) * mm, "end": v(135.82, 550.64) * mm});
            skPoint(sketch, "E274.visualSharp", {"position": v(-129.03, 590.64) * mm});
            skArc(sketch, "E274.filletArc", {"start": v(-126.03, 590.64) * mm, "mid": v(-128.15, 589.76) * mm, "end": v(-129.03, 587.64) * mm});
            skPoint(sketch, "E275.visualSharp", {"position": v(-129.03, 540.64) * mm});
            skArc(sketch, "E275.filletArc", {"start": v(-129.03, 543.64) * mm, "mid": v(-128.15, 541.52) * mm, "end": v(-126.03, 540.64) * mm});
            skLineSegment(sketch, "E276.bottom", {"start": v(122.47, 587.64) * mm, "end": v(103.97, 587.64) * mm});
            skLineSegment(sketch, "E276.top", {"start": v(122.47, 586.14) * mm, "end": v(103.97, 586.14) * mm});
            skLineSegment(sketch, "E276.left", {"start": v(123.22, 586.9) * mm, "end": v(123.22, 586.9) * mm});
            skLineSegment(sketch, "E276.right", {"start": v(103.22, 586.9) * mm, "end": v(103.22, 586.9) * mm});
            skCircle(sketch, "E277", {"center": v(-107.28, 575.63) * mm, "radius": 1 * mm});
            skCircle(sketch, "E278", {"center": v(-100.86, 579.64) * mm, "radius": 1 * mm});
            skCircle(sketch, "E279", {"center": v(-67.28, 555.66) * mm, "radius": 1 * mm});
            skCircle(sketch, "E280", {"center": v(-73.7, 551.64) * mm, "radius": 1 * mm});
            skCircle(sketch, "E281", {"center": v(-21.7, 579.64) * mm, "radius": 1 * mm});
            skCircle(sketch, "E282", {"center": v(-55.28, 555.66) * mm, "radius": 1 * mm});
            skCircle(sketch, "E283", {"center": v(-48.86, 551.64) * mm, "radius": 1 * mm});
            skCircle(sketch, "E284", {"center": v(-15.28, 575.63) * mm, "radius": 1 * mm});
            skCircle(sketch, "E285", {"center": v(49.22, 555.66) * mm, "radius": 1 * mm});
            skCircle(sketch, "E286", {"center": v(82.8, 579.64) * mm, "radius": 1 * mm});
            skCircle(sketch, "E287", {"center": v(55.64, 551.64) * mm, "radius": 1 * mm});
            skCircle(sketch, "E288", {"center": v(89.22, 575.63) * mm, "radius": 1 * mm});
            skCircle(sketch, "E289", {"center": v(101.22, 575.5) * mm, "radius": 1 * mm});
            skCircle(sketch, "E290", {"center": v(132.83, 551.64) * mm, "radius": 1 * mm});
            skCircle(sketch, "E291", {"center": v(107.35, 579.64) * mm, "radius": 1 * mm});
            skCircle(sketch, "E292", {"center": v(141.22, 554.08) * mm, "radius": 1 * mm});
            skPoint(sketch, "E293.visualSharp", {"position": v(-66.28, 580.64) * mm});
            skArc(sketch, "E293.filletArc", {"start": v(-66.28, 578.64) * mm, "mid": v(-66.87, 580.06) * mm, "end": v(-68.28, 580.64) * mm});
            skPoint(sketch, "E294.visualSharp", {"position": v(-108.28, 550.64) * mm});
            skArc(sketch, "E294.filletArc", {"start": v(-108.28, 552.64) * mm, "mid": v(-107.7, 551.23) * mm, "end": v(-106.28, 550.64) * mm});
            skPoint(sketch, "E295.visualSharp", {"position": v(-56.28, 580.64) * mm});
            skArc(sketch, "E295.filletArc", {"start": v(-54.28, 580.64) * mm, "mid": v(-55.7, 580.06) * mm, "end": v(-56.28, 578.64) * mm});
            skPoint(sketch, "E296.visualSharp", {"position": v(-14.28, 550.64) * mm});
            skArc(sketch, "E296.filletArc", {"start": v(-16.28, 550.64) * mm, "mid": v(-14.87, 551.23) * mm, "end": v(-14.28, 552.64) * mm});
            skPoint(sketch, "E297.visualSharp", {"position": v(48.22, 580.64) * mm});
            skArc(sketch, "E297.filletArc", {"start": v(50.22, 580.64) * mm, "mid": v(48.8, 580.06) * mm, "end": v(48.22, 578.64) * mm});
            skPoint(sketch, "E298.visualSharp", {"position": v(90.22, 550.64) * mm});
            skArc(sketch, "E298.filletArc", {"start": v(86.22, 550.64) * mm, "mid": v(89.05, 551.81) * mm, "end": v(90.22, 554.64) * mm});
            skPoint(sketch, "E299.visualSharp", {"position": v(100.22, 550.64) * mm});
            skArc(sketch, "E299.filletArc", {"start": v(100.22, 554.64) * mm, "mid": v(101.39, 551.81) * mm, "end": v(104.22, 550.64) * mm});
            skPoint(sketch, "E300.visualSharp", {"position": v(142.22, 580.64) * mm});
            skArc(sketch, "E300.filletArc", {"start": v(142.22, 578.64) * mm, "mid": v(141.63, 580.06) * mm, "end": v(140.22, 580.64) * mm});
            skLineSegment(sketch, "E301.bottom", {"start": v(86.47, 586.14) * mm, "end": v(67.97, 586.14) * mm});
            skLineSegment(sketch, "E301.top", {"start": v(86.47, 587.64) * mm, "end": v(67.97, 587.64) * mm});
            skLineSegment(sketch, "E301.left", {"start": v(87.22, 586.9) * mm, "end": v(87.22, 586.9) * mm});
            skLineSegment(sketch, "E301.right", {"start": v(67.22, 586.9) * mm, "end": v(67.22, 586.9) * mm});
            skPoint(sketch, "E302.visualSharp", {"position": v(67.22, 587.64) * mm});
            skArc(sketch, "E302.filletArc", {"start": v(67.97, 587.64) * mm, "mid": v(67.44, 587.42) * mm, "end": v(67.22, 586.9) * mm});
            skPoint(sketch, "E303.visualSharp", {"position": v(67.22, 586.14) * mm});
            skArc(sketch, "E303.filletArc", {"start": v(67.22, 586.9) * mm, "mid": v(67.44, 586.36) * mm, "end": v(67.97, 586.14) * mm});
            skPoint(sketch, "E304.visualSharp", {"position": v(87.22, 587.64) * mm});
            skArc(sketch, "E304.filletArc", {"start": v(87.22, 586.9) * mm, "mid": v(87, 587.42) * mm, "end": v(86.47, 587.64) * mm});
            skPoint(sketch, "E305.visualSharp", {"position": v(87.22, 586.14) * mm});
            skArc(sketch, "E305.filletArc", {"start": v(86.47, 586.14) * mm, "mid": v(87, 586.36) * mm, "end": v(87.22, 586.9) * mm});
            skPoint(sketch, "E306.visualSharp", {"position": v(103.22, 587.64) * mm});
            skArc(sketch, "E306.filletArc", {"start": v(103.97, 587.64) * mm, "mid": v(103.44, 587.42) * mm, "end": v(103.22, 586.9) * mm});
            skPoint(sketch, "E307.visualSharp", {"position": v(103.22, 586.14) * mm});
            skArc(sketch, "E307.filletArc", {"start": v(103.22, 586.9) * mm, "mid": v(103.44, 586.36) * mm, "end": v(103.97, 586.14) * mm});
            skPoint(sketch, "E308.visualSharp", {"position": v(123.22, 587.64) * mm});
            skArc(sketch, "E308.filletArc", {"start": v(123.22, 586.9) * mm, "mid": v(123, 587.42) * mm, "end": v(122.47, 587.64) * mm});
            skPoint(sketch, "E309.visualSharp", {"position": v(123.22, 586.14) * mm});
            skArc(sketch, "E309.filletArc", {"start": v(122.47, 586.14) * mm, "mid": v(123, 586.36) * mm, "end": v(123.22, 586.9) * mm});
            skArc(sketch, "E310.MirrorCS", {"start": v(123.22, 544.4) * mm, "mid": v(123, 543.86) * mm, "end": v(122.47, 543.64) * mm});
            skArc(sketch, "E311.MirrorCS", {"start": v(103.97, 543.64) * mm, "mid": v(103.44, 543.86) * mm, "end": v(103.22, 544.4) * mm});
            skArc(sketch, "E312.MirrorCS", {"start": v(122.47, 545.14) * mm, "mid": v(123, 544.92) * mm, "end": v(123.22, 544.4) * mm});
            skArc(sketch, "E313.MirrorCS", {"start": v(103.22, 544.4) * mm, "mid": v(103.44, 544.92) * mm, "end": v(103.97, 545.14) * mm});
            skLineSegment(sketch, "E314.MirrorCS", {"start": v(123.22, 544.4) * mm, "end": v(123.22, 544.4) * mm});
            skLineSegment(sketch, "E315.MirrorCS", {"start": v(103.22, 544.4) * mm, "end": v(103.22, 544.4) * mm});
            skPoint(sketch, "E316.MirrorP", {"position": v(123.22, 543.64) * mm});
            skPoint(sketch, "E317.MirrorP", {"position": v(103.22, 543.64) * mm});
            skLineSegment(sketch, "E318.MirrorCS", {"start": v(122.47, 543.64) * mm, "end": v(103.97, 543.64) * mm});
            skLineSegment(sketch, "E319.MirrorCS", {"start": v(122.47, 545.14) * mm, "end": v(103.97, 545.14) * mm});
            skPoint(sketch, "E320.MirrorP", {"position": v(123.22, 545.14) * mm});
            skPoint(sketch, "E321.MirrorP", {"position": v(103.22, 545.14) * mm});
            skArc(sketch, "E322.MirrorCS", {"start": v(87.22, 544.4) * mm, "mid": v(87, 543.86) * mm, "end": v(86.47, 543.64) * mm});
            skArc(sketch, "E323.MirrorCS", {"start": v(67.97, 543.64) * mm, "mid": v(67.44, 543.86) * mm, "end": v(67.22, 544.4) * mm});
            skArc(sketch, "E324.MirrorCS", {"start": v(86.47, 545.14) * mm, "mid": v(87, 544.92) * mm, "end": v(87.22, 544.4) * mm});
            skArc(sketch, "E325.MirrorCS", {"start": v(67.22, 544.4) * mm, "mid": v(67.44, 544.92) * mm, "end": v(67.97, 545.14) * mm});
            skLineSegment(sketch, "E326.MirrorCS", {"start": v(87.22, 544.4) * mm, "end": v(87.22, 544.4) * mm});
            skLineSegment(sketch, "E327.MirrorCS", {"start": v(67.22, 544.4) * mm, "end": v(67.22, 544.4) * mm});
            skPoint(sketch, "E328.MirrorP", {"position": v(87.22, 543.64) * mm});
            skPoint(sketch, "E329.MirrorP", {"position": v(67.22, 543.64) * mm});
            skLineSegment(sketch, "E330.MirrorCS", {"start": v(86.47, 543.64) * mm, "end": v(67.97, 543.64) * mm});
            skLineSegment(sketch, "E331.MirrorCS", {"start": v(86.47, 545.14) * mm, "end": v(67.97, 545.14) * mm});
            skPoint(sketch, "E332.MirrorP", {"position": v(87.22, 545.14) * mm});
            skPoint(sketch, "E333.MirrorP", {"position": v(67.22, 545.14) * mm});
            skCircle(sketch, "E334", {"center": v(-89.53, 545.64) * mm, "radius": 7 * mm});
            skCircle(sketch, "E335", {"center": v(-89.53, 545.64) * mm, "radius": 3 * mm});
            skCircle(sketch, "E336", {"center": v(-84.24, 551.64) * mm, "radius": 1 * mm});
            skCircle(sketch, "E337", {"center": v(-94.82, 551.64) * mm, "radius": 1 * mm});
            skCircle(sketch, "E338", {"center": v(-94.82, 539.64) * mm, "radius": 1 * mm});
            skCircle(sketch, "E339", {"center": v(-84.24, 539.64) * mm, "radius": 1 * mm});
            skCircle(sketch, "E340.MirrorC", {"center": v(-89.53, 585.64) * mm, "radius": 7 * mm});
            skCircle(sketch, "E341.MirrorC", {"center": v(-89.53, 585.64) * mm, "radius": 3 * mm});
            skCircle(sketch, "E342.MirrorC", {"center": v(-94.82, 579.64) * mm, "radius": 1 * mm});
            skCircle(sketch, "E343.MirrorC", {"center": v(-84.24, 579.64) * mm, "radius": 1 * mm});
            skCircle(sketch, "E344.MirrorC", {"center": v(-84.24, 591.64) * mm, "radius": 1 * mm});
            skCircle(sketch, "E345.MirrorC", {"center": v(-94.82, 591.64) * mm, "radius": 1 * mm});
            skCircle(sketch, "E346", {"center": v(95.22, 583.14) * mm, "radius": 3 * mm});
            skCircle(sketch, "E347.MirrorC", {"center": v(95.22, 548.14) * mm, "radius": 3 * mm});
            skCircle(sketch, "E348", {"center": v(-13.28, 585.64) * mm, "radius": 1.5 * mm});
            skCircle(sketch, "E349.MirrorC", {"center": v(-13.28, 545.64) * mm, "radius": 1.5 * mm});
            skCircle(sketch, "E350", {"center": v(-112.03, 585.64) * mm, "radius": 1.5 * mm});
            skCircle(sketch, "E351.MirrorC", {"center": v(-112.03, 545.64) * mm, "radius": 1.5 * mm});
            skLineSegment(sketch, "E352", {"start": v(-118.03, 586.14) * mm, "end": v(-118.03, 545.14) * mm});
            skArc(sketch, "E353.filletArc", {"start": v(-113.53, 590.64) * mm, "mid": v(-116.71, 589.32) * mm, "end": v(-118.03, 586.14) * mm});
            skArc(sketch, "E354.filletArc", {"start": v(-118.03, 545.14) * mm, "mid": v(-116.71, 541.96) * mm, "end": v(-113.53, 540.64) * mm});
            skSolve(sketch);
        }
        {
            var Q0;
            {var subQ0=sQuery(id+"F2.wireOp",EDGE,"E339");var subQ1=sQuery(id+"F2.wireOp",EDGE,"E214.top");var subQ2=makeQuery(id+"F2.imprint","INTERSECT",VERTEX,{"derivedFrom":[subQ1,subQ0]});Q0=makeQuery(id+"F2.imprint","IMPRINT",FACE,{"disambiguationData":[TD([[makeQuery(id+"F2.imprint","IMPRINT",EDGE,{"disambiguationData":[TD([[subQ2,-1.0]])],"derivedFrom":subQ1}),1.0]])]});}
            var Q1;
            {var subQ0=sQuery(id+"F2.wireOp",EDGE,"E334");var subQ1=sQuery(id+"F2.wireOp",EDGE,"E214.top");var subQ2=makeQuery(id+"F2.imprint","INTERSECT",VERTEX,{"disambiguationData":[OD(0.0)],"derivedFrom":[subQ1,subQ0]});Q1=makeQuery(id+"F2.imprint","IMPRINT",FACE,{"disambiguationData":[TD([[makeQuery(id+"F2.imprint","IMPRINT",EDGE,{"disambiguationData":[TD([[subQ2,-1.0]])],"derivedFrom":subQ1}),1.0]])]});}
            var Q2;
            {var subQ0=sQuery(id+"F2.wireOp",EDGE,"E338");var subQ1=sQuery(id+"F2.wireOp",EDGE,"E214.top");var subQ2=makeQuery(id+"F2.imprint","INTERSECT",VERTEX,{"derivedFrom":[subQ1,subQ0]});Q2=makeQuery(id+"F2.imprint","IMPRINT",FACE,{"disambiguationData":[TD([[makeQuery(id+"F2.imprint","IMPRINT",EDGE,{"disambiguationData":[TD([[subQ2,1.0]])],"derivedFrom":subQ1}),1.0]])]});}
            var Q3;
            Q3=makeQuery(id+"F2.imprint","IMPRINT",FACE,{"disambiguationData":[TD([[makeQuery(id+"F2.imprint","IMPRINT",EDGE,{"derivedFrom":sQuery(id+"F2.wireOp",EDGE,"E225.MirrorC")}),1.0]])]});
            var Q4;
            Q4=makeQuery(id+"F2.imprint","IMPRINT",FACE,{"disambiguationData":[TD([[makeQuery(id+"F2.imprint","IMPRINT",EDGE,{"derivedFrom":sQuery(id+"F2.wireOp",EDGE,"E214.bottom")}),1.0]])]});
            var Q5;
            Q5=makeQuery(id+"F2.imprint","IMPRINT",FACE,{"disambiguationData":[TD([[makeQuery(id+"F2.imprint","IMPRINT",EDGE,{"derivedFrom":sQuery(id+"F2.wireOp",EDGE,"E222.MirrorC")}),1.0]])]});
            var Q6;
            {var subQ13=sQuery(id+"F2.wireOp",EDGE,"E219");var subQ16=sQuery(id+"F2.wireOp",EDGE,"E228.right");var subQ18=makeQuery(id+"F2.imprint","INTERSECT",VERTEX,{"derivedFrom":[subQ13,subQ16]});Q6=makeQuery(id+"F2.imprint","IMPRINT",FACE,{"disambiguationData":[TD([[makeQuery(id+"F2.imprint","IMPRINT",EDGE,{"disambiguationData":[TD([[subQ18,-1.0]])],"derivedFrom":subQ13}),-1.0]])]});}
            var Q7;
            {var subQ0=sQuery(id+"F2.wireOp",EDGE,"E244");var subQ1=sQuery(id+"F2.wireOp",EDGE,"E241.left");var subQ2=makeQuery(id+"F2.imprint","INTERSECT",VERTEX,{"derivedFrom":[subQ1,subQ0]});Q7=makeQuery(id+"F2.imprint","IMPRINT",FACE,{"disambiguationData":[TD([[makeQuery(id+"F2.imprint","IMPRINT",EDGE,{"disambiguationData":[TD([[subQ2,-1.0]])],"derivedFrom":subQ0}),1.0]])]});}
            var Q8;
            {var subQ0=sQuery(id+"F2.wireOp",EDGE,"E243");var subQ3=sQuery(id+"F2.wireOp",EDGE,"E241.bottom");var subQ4=makeQuery(id+"F2.imprint","INTERSECT",VERTEX,{"derivedFrom":[subQ3,subQ0]});Q8=makeQuery(id+"F2.imprint","IMPRINT",FACE,{"disambiguationData":[TD([[makeQuery(id+"F2.imprint","IMPRINT",EDGE,{"disambiguationData":[TD([[subQ4,-1.0]])],"derivedFrom":subQ0}),-1.0]])]});}
            var Q9;
            {var subQ0=sQuery(id+"F2.wireOp",EDGE,"E246");var subQ5=sQuery(id+"F2.wireOp",EDGE,"E243");var subQ6=makeQuery(id+"F2.imprint","INTERSECT",VERTEX,{"derivedFrom":[subQ5,subQ0]});Q9=makeQuery(id+"F2.imprint","IMPRINT",FACE,{"disambiguationData":[TD([[makeQuery(id+"F2.imprint","IMPRINT",EDGE,{"disambiguationData":[TD([[subQ6,-1.0]])],"derivedFrom":subQ5}),-1.0]])]});}
            var Q10;
            {var subQ0=sQuery(id+"F2.wireOp",EDGE,"E243");var subQ3=sQuery(id+"F2.wireOp",EDGE,"E245");var subQ5=makeQuery(id+"F2.imprint","INTERSECT",VERTEX,{"derivedFrom":[subQ0,subQ3]});Q10=makeQuery(id+"F2.imprint","IMPRINT",FACE,{"disambiguationData":[TD([[makeQuery(id+"F2.imprint","IMPRINT",EDGE,{"disambiguationData":[TD([[subQ5,-1.0]])],"derivedFrom":subQ0}),-1.0]])]});}
            var Q11;
            {var subQ0=sQuery(id+"F2.wireOp",EDGE,"E242");var subQ3=sQuery(id+"F2.wireOp",EDGE,"E246");var subQ5=makeQuery(id+"F2.imprint","INTERSECT",VERTEX,{"derivedFrom":[subQ0,subQ3]});Q11=makeQuery(id+"F2.imprint","IMPRINT",FACE,{"disambiguationData":[TD([[makeQuery(id+"F2.imprint","IMPRINT",EDGE,{"disambiguationData":[TD([[subQ5,-1.0]])],"derivedFrom":subQ0}),-1.0]])]});}
            var Q12;
            {var subQ3=sQuery(id+"F2.wireOp",EDGE,"E243");var subQ5=sQuery(id+"F2.wireOp",EDGE,"E246");var subQ6=makeQuery(id+"F2.imprint","INTERSECT",VERTEX,{"derivedFrom":[subQ3,subQ5]});Q12=makeQuery(id+"F2.imprint","IMPRINT",FACE,{"disambiguationData":[TD([[makeQuery(id+"F2.imprint","IMPRINT",EDGE,{"disambiguationData":[TD([[subQ6,-1.0]])],"derivedFrom":subQ3}),1.0]])]});}
            var Q13;
            {var subQ0=sQuery(id+"F2.wireOp",EDGE,"E247");var subQ1=makeQuery(id+"F2.imprint","INTERSECT",VERTEX,{"derivedFrom":[subQ0,sQuery(id+"F2.wireOp",EDGE,"E252")]});Q13=makeQuery(id+"F2.imprint","IMPRINT",FACE,{"disambiguationData":[TD([[makeQuery(id+"F2.imprint","IMPRINT",EDGE,{"disambiguationData":[TD([[subQ1,-1.0]])],"derivedFrom":subQ0}),1.0]])]});}
            var Q14;
            {var subQ0=sQuery(id+"F2.wireOp",EDGE,"E243");var subQ1=makeQuery(id+"F2.imprint","INTERSECT",VERTEX,{"derivedFrom":[subQ0,sQuery(id+"F2.wireOp",EDGE,"E252")]});Q14=makeQuery(id+"F2.imprint","IMPRINT",FACE,{"disambiguationData":[TD([[makeQuery(id+"F2.imprint","IMPRINT",EDGE,{"disambiguationData":[TD([[subQ1,-1.0]])],"derivedFrom":subQ0}),-1.0]])]});}
            var Q15;
            {var subQ0=sQuery(id+"F2.wireOp",EDGE,"E244");var subQ3=sQuery(id+"F2.wireOp",EDGE,"E247");var subQ4=makeQuery(id+"F2.imprint","INTERSECT",VERTEX,{"derivedFrom":[subQ0,subQ3]});Q15=makeQuery(id+"F2.imprint","IMPRINT",FACE,{"disambiguationData":[TD([[makeQuery(id+"F2.imprint","IMPRINT",EDGE,{"disambiguationData":[TD([[subQ4,-1.0]])],"derivedFrom":subQ0}),1.0]])]});}
            var Q16;
            {var subQ3=sQuery(id+"F2.wireOp",EDGE,"E245");var subQ5=sQuery(id+"F2.wireOp",EDGE,"E244");var subQ6=makeQuery(id+"F2.imprint","INTERSECT",VERTEX,{"derivedFrom":[subQ5,subQ3]});Q16=makeQuery(id+"F2.imprint","IMPRINT",FACE,{"disambiguationData":[TD([[makeQuery(id+"F2.imprint","IMPRINT",EDGE,{"disambiguationData":[TD([[subQ6,-1.0]])],"derivedFrom":subQ5}),1.0]])]});}
            var Q17;
            {var subQ0=sQuery(id+"F2.wireOp",EDGE,"E245");var subQ3=sQuery(id+"F2.wireOp",EDGE,"E244");var subQ5=makeQuery(id+"F2.imprint","INTERSECT",VERTEX,{"derivedFrom":[subQ3,subQ0]});Q17=makeQuery(id+"F2.imprint","IMPRINT",FACE,{"disambiguationData":[TD([[makeQuery(id+"F2.imprint","IMPRINT",EDGE,{"disambiguationData":[TD([[subQ5,1.0]])],"derivedFrom":subQ3}),1.0]])]});}
            var Q18;
            {var subQ0=sQuery(id+"F2.wireOp",EDGE,"E247");var subQ3=sQuery(id+"F2.wireOp",EDGE,"E242");var subQ5=makeQuery(id+"F2.imprint","INTERSECT",VERTEX,{"derivedFrom":[subQ3,subQ0]});Q18=makeQuery(id+"F2.imprint","IMPRINT",FACE,{"disambiguationData":[TD([[makeQuery(id+"F2.imprint","IMPRINT",EDGE,{"disambiguationData":[TD([[subQ5,1.0]])],"derivedFrom":subQ3}),1.0]])]});}
            var Q19;
            {var subQ4=sQuery(id+"F2.wireOp",EDGE,"E245");var subQ6=sQuery(id+"F2.wireOp",EDGE,"E244");var subQ7=makeQuery(id+"F2.imprint","INTERSECT",VERTEX,{"derivedFrom":[subQ6,subQ4]});Q19=makeQuery(id+"F2.imprint","IMPRINT",FACE,{"disambiguationData":[TD([[makeQuery(id+"F2.imprint","IMPRINT",EDGE,{"disambiguationData":[TD([[subQ7,-1.0]])],"derivedFrom":subQ6}),-1.0]])]});}
            var Q20;
            {var subQ0=sQuery(id+"F2.wireOp",EDGE,"E246");var subQ1=sQuery(id+"F2.wireOp",EDGE,"E241.left");var subQ2=makeQuery(id+"F2.imprint","INTERSECT",VERTEX,{"derivedFrom":[subQ1,subQ0]});Q20=makeQuery(id+"F2.imprint","IMPRINT",FACE,{"disambiguationData":[TD([[makeQuery(id+"F2.imprint","IMPRINT",EDGE,{"disambiguationData":[TD([[subQ2,-1.0]])],"derivedFrom":subQ0}),-1.0]])]});}
            var Q21;
            {var subQ0=sQuery(id+"F2.wireOp",EDGE,"E246");var subQ1=sQuery(id+"F2.wireOp",EDGE,"E241.left");var subQ2=makeQuery(id+"F2.imprint","INTERSECT",VERTEX,{"derivedFrom":[subQ1,subQ0]});Q21=makeQuery(id+"F2.imprint","IMPRINT",FACE,{"disambiguationData":[TD([[makeQuery(id+"F2.imprint","IMPRINT",EDGE,{"disambiguationData":[TD([[subQ2,1.0]])],"derivedFrom":subQ1}),1.0]])]});}
            var Q22;
            {var subQ0=sQuery(id+"F2.wireOp",EDGE,"E247");var subQ1=sQuery(id+"F2.wireOp",EDGE,"E241.top");var subQ2=makeQuery(id+"F2.imprint","INTERSECT",VERTEX,{"derivedFrom":[subQ1,subQ0]});Q22=makeQuery(id+"F2.imprint","IMPRINT",FACE,{"disambiguationData":[TD([[makeQuery(id+"F2.imprint","IMPRINT",EDGE,{"disambiguationData":[TD([[subQ2,-1.0]])],"derivedFrom":subQ1}),1.0]])]});}
            var Q23;
            {var subQ0=sQuery(id+"F2.wireOp",EDGE,"E246");var subQ1=sQuery(id+"F2.wireOp",EDGE,"E241.bottom");var subQ2=makeQuery(id+"F2.imprint","INTERSECT",VERTEX,{"derivedFrom":[subQ1,subQ0]});Q23=makeQuery(id+"F2.imprint","IMPRINT",FACE,{"disambiguationData":[TD([[makeQuery(id+"F2.imprint","IMPRINT",EDGE,{"disambiguationData":[TD([[subQ2,1.0]])],"derivedFrom":subQ1}),-1.0]])]});}
            var Q24;
            {var subQ0=sQuery(id+"F2.wireOp",EDGE,"E247");var subQ1=sQuery(id+"F2.wireOp",EDGE,"E241.right");var subQ2=makeQuery(id+"F2.imprint","INTERSECT",VERTEX,{"derivedFrom":[subQ1,subQ0]});Q24=makeQuery(id+"F2.imprint","IMPRINT",FACE,{"disambiguationData":[TD([[makeQuery(id+"F2.imprint","IMPRINT",EDGE,{"disambiguationData":[TD([[subQ2,-1.0]])],"derivedFrom":subQ1}),-1.0]])]});}
            var Q25;
            {var subQ0=sQuery(id+"F2.wireOp",EDGE,"E244");var subQ1=sQuery(id+"F2.wireOp",EDGE,"E241.top");var subQ2=makeQuery(id+"F2.imprint","INTERSECT",VERTEX,{"derivedFrom":[subQ1,subQ0]});Q25=makeQuery(id+"F2.imprint","IMPRINT",FACE,{"disambiguationData":[TD([[makeQuery(id+"F2.imprint","IMPRINT",EDGE,{"disambiguationData":[TD([[subQ2,1.0]])],"derivedFrom":subQ1}),1.0]])]});}
            var Q26;
            {var subQ13=sQuery(id+"F2.wireOp",EDGE,"E228.right");var subQ17=sQuery(id+"F2.wireOp",EDGE,"E219");var subQ18=makeQuery(id+"F2.imprint","INTERSECT",VERTEX,{"derivedFrom":[subQ17,subQ13]});Q26=makeQuery(id+"F2.imprint","IMPRINT",FACE,{"disambiguationData":[TD([[makeQuery(id+"F2.imprint","IMPRINT",EDGE,{"disambiguationData":[TD([[subQ18,-1.0]])],"derivedFrom":subQ17}),1.0]])]});}
            var Q27;
            {var subQ0=sQuery(id+"F2.wireOp",EDGE,"E243");var subQ1=sQuery(id+"F2.wireOp",EDGE,"E241.right");var subQ2=makeQuery(id+"F2.imprint","INTERSECT",VERTEX,{"derivedFrom":[subQ1,subQ0]});Q27=makeQuery(id+"F2.imprint","IMPRINT",FACE,{"disambiguationData":[TD([[makeQuery(id+"F2.imprint","IMPRINT",EDGE,{"disambiguationData":[TD([[subQ2,1.0]])],"derivedFrom":subQ1}),-1.0]])]});}
            var Q28;
            {var subQ0=sQuery(id+"F2.wireOp",EDGE,"E244");var subQ1=sQuery(id+"F2.wireOp",EDGE,"E241.left");var subQ2=makeQuery(id+"F2.imprint","INTERSECT",VERTEX,{"derivedFrom":[subQ1,subQ0]});Q28=makeQuery(id+"F2.imprint","IMPRINT",FACE,{"disambiguationData":[TD([[makeQuery(id+"F2.imprint","IMPRINT",EDGE,{"disambiguationData":[TD([[subQ2,-1.0]])],"derivedFrom":subQ1}),1.0]])]});}
            var Q29;
            {var subQ0=sQuery(id+"F2.wireOp",EDGE,"E243");var subQ1=sQuery(id+"F2.wireOp",EDGE,"E241.bottom");var subQ2=makeQuery(id+"F2.imprint","INTERSECT",VERTEX,{"derivedFrom":[subQ1,subQ0]});Q29=makeQuery(id+"F2.imprint","IMPRINT",FACE,{"disambiguationData":[TD([[makeQuery(id+"F2.imprint","IMPRINT",EDGE,{"disambiguationData":[TD([[subQ2,-1.0]])],"derivedFrom":subQ1}),-1.0]])]});}
            var Q30;
            {var subQ0=sQuery(id+"F2.wireOp",EDGE,"E254");var subQ1=sQuery(id+"F2.wireOp",EDGE,"E219");var subQ2=makeQuery(id+"F2.imprint","INTERSECT",VERTEX,{"disambiguationData":[OD(0.0)],"derivedFrom":[subQ1,subQ0]});Q30=makeQuery(id+"F2.imprint","IMPRINT",FACE,{"disambiguationData":[TD([[makeQuery(id+"F2.imprint","IMPRINT",EDGE,{"disambiguationData":[TD([[subQ2,-1.0]])],"derivedFrom":subQ0}),-1.0]])]});}
            var Q31;
            {var subQ0=sQuery(id+"F2.wireOp",EDGE,"E254");var subQ1=sQuery(id+"F2.wireOp",EDGE,"E219");var subQ2=makeQuery(id+"F2.imprint","INTERSECT",VERTEX,{"disambiguationData":[OD(0.0)],"derivedFrom":[subQ1,subQ0]});Q31=makeQuery(id+"F2.imprint","IMPRINT",FACE,{"disambiguationData":[TD([[makeQuery(id+"F2.imprint","IMPRINT",EDGE,{"disambiguationData":[TD([[subQ2,1.0]])],"derivedFrom":subQ0}),-1.0]])]});}
            var Q32;
            {var subQ0=sQuery(id+"F2.wireOp",EDGE,"E252");var subQ1=sQuery(id+"F2.wireOp",EDGE,"E219");var subQ2=makeQuery(id+"F2.imprint","INTERSECT",VERTEX,{"disambiguationData":[OD(1.0)],"derivedFrom":[subQ1,subQ0]});Q32=makeQuery(id+"F2.imprint","IMPRINT",FACE,{"disambiguationData":[TD([[makeQuery(id+"F2.imprint","IMPRINT",EDGE,{"disambiguationData":[TD([[subQ2,1.0]])],"derivedFrom":subQ0}),-1.0]])]});}
            var Q33;
            {var subQ0=sQuery(id+"F2.wireOp",EDGE,"E252");var subQ1=sQuery(id+"F2.wireOp",EDGE,"E219");var subQ2=makeQuery(id+"F2.imprint","INTERSECT",VERTEX,{"disambiguationData":[OD(1.0)],"derivedFrom":[subQ1,subQ0]});Q33=makeQuery(id+"F2.imprint","IMPRINT",FACE,{"disambiguationData":[TD([[makeQuery(id+"F2.imprint","IMPRINT",EDGE,{"disambiguationData":[TD([[subQ2,-1.0]])],"derivedFrom":subQ0}),-1.0]])]});}
            var Q34;
            {var subQ0=sQuery(id+"F2.wireOp",EDGE,"E249");var subQ1=sQuery(id+"F2.wireOp",EDGE,"E243");var subQ2=makeQuery(id+"F2.imprint","INTERSECT",VERTEX,{"derivedFrom":[subQ1,subQ0]});Q34=makeQuery(id+"F2.imprint","IMPRINT",FACE,{"disambiguationData":[TD([[makeQuery(id+"F2.imprint","IMPRINT",EDGE,{"disambiguationData":[TD([[subQ2,-1.0]])],"derivedFrom":subQ1}),1.0]])]});}
            var Q35;
            {var subQ0=sQuery(id+"F2.wireOp",EDGE,"E247");var subQ1=sQuery(id+"F2.wireOp",EDGE,"E244");var subQ2=makeQuery(id+"F2.imprint","INTERSECT",VERTEX,{"derivedFrom":[subQ1,subQ0]});Q35=makeQuery(id+"F2.imprint","IMPRINT",FACE,{"disambiguationData":[TD([[makeQuery(id+"F2.imprint","IMPRINT",EDGE,{"disambiguationData":[TD([[subQ2,-1.0]])],"derivedFrom":subQ1}),-1.0]])]});}
            var Q36;
            Q36=makeQuery(id+"F2.imprint","IMPRINT",FACE,{"disambiguationData":[TD([[makeQuery(id+"F2.imprint","IMPRINT",EDGE,{"derivedFrom":sQuery(id+"F2.wireOp",EDGE,"E217")}),1.0]])]});
            var Q37;
            Q37=makeQuery(id+"F2.imprint","IMPRINT",FACE,{"disambiguationData":[TD([[makeQuery(id+"F2.imprint","IMPRINT",EDGE,{"derivedFrom":sQuery(id+"F2.wireOp",EDGE,"E226.MirrorC")}),-1.0]])]});
            var Q38;
            {var subQ0=sQuery(id+"F2.wireOp",EDGE,"E270");var subQ6=sQuery(id+"F2.wireOp",EDGE,"E219");var subQ8=makeQuery(id+"F2.imprint","INTERSECT",VERTEX,{"derivedFrom":[subQ6,subQ0]});Q38=makeQuery(id+"F2.imprint","IMPRINT",FACE,{"disambiguationData":[TD([[makeQuery(id+"F2.imprint","IMPRINT",EDGE,{"disambiguationData":[TD([[subQ8,-1.0]])],"derivedFrom":subQ6}),-1.0]])]});}
            var Q39;
            {var subQ0=sQuery(id+"F2.wireOp",EDGE,"E268");var subQ3=sQuery(id+"F2.wireOp",EDGE,"E219");var subQ4=makeQuery(id+"F2.imprint","INTERSECT",VERTEX,{"derivedFrom":[subQ3,subQ0]});Q39=makeQuery(id+"F2.imprint","IMPRINT",FACE,{"disambiguationData":[TD([[makeQuery(id+"F2.imprint","IMPRINT",EDGE,{"disambiguationData":[TD([[subQ4,-1.0]])],"derivedFrom":subQ3}),-1.0]])]});}
            var Q40;
            {var subQ0=sQuery(id+"F2.wireOp",EDGE,"E270");var subQ1=sQuery(id+"F2.wireOp",EDGE,"E219");var subQ2=makeQuery(id+"F2.imprint","INTERSECT",VERTEX,{"derivedFrom":[subQ1,subQ0]});Q40=makeQuery(id+"F2.imprint","IMPRINT",FACE,{"disambiguationData":[TD([[makeQuery(id+"F2.imprint","IMPRINT",EDGE,{"disambiguationData":[TD([[subQ2,-1.0]])],"derivedFrom":subQ1}),1.0]])]});}
            var Q41;
            {var subQ0=sQuery(id+"F2.wireOp",EDGE,"E268");var subQ3=sQuery(id+"F2.wireOp",EDGE,"E219");var subQ4=makeQuery(id+"F2.imprint","INTERSECT",VERTEX,{"derivedFrom":[subQ3,subQ0]});Q41=makeQuery(id+"F2.imprint","IMPRINT",FACE,{"disambiguationData":[TD([[makeQuery(id+"F2.imprint","IMPRINT",EDGE,{"disambiguationData":[TD([[subQ4,-1.0]])],"derivedFrom":subQ3}),1.0]])]});}
            var Q42;
            {var subQ4=sQuery(id+"F2.wireOp",EDGE,"E271");var subQ6=sQuery(id+"F2.wireOp",EDGE,"E219");var subQ7=makeQuery(id+"F2.imprint","INTERSECT",VERTEX,{"derivedFrom":[subQ6,subQ4]});Q42=makeQuery(id+"F2.imprint","IMPRINT",FACE,{"disambiguationData":[TD([[makeQuery(id+"F2.imprint","IMPRINT",EDGE,{"disambiguationData":[TD([[subQ7,-1.0]])],"derivedFrom":subQ6}),-1.0]])]});}
            var Q43;
            {var subQ0=sQuery(id+"F2.wireOp",EDGE,"E272");var subQ6=sQuery(id+"F2.wireOp",EDGE,"E219");var subQ8=makeQuery(id+"F2.imprint","INTERSECT",VERTEX,{"derivedFrom":[subQ6,subQ0]});Q43=makeQuery(id+"F2.imprint","IMPRINT",FACE,{"disambiguationData":[TD([[makeQuery(id+"F2.imprint","IMPRINT",EDGE,{"disambiguationData":[TD([[subQ8,-1.0]])],"derivedFrom":subQ6}),-1.0]])]});}
            var Q44;
            {var subQ1=sQuery(id+"F2.wireOp",EDGE,"E219");var subQ4=sQuery(id+"F2.wireOp",EDGE,"E271");var subQ7=makeQuery(id+"F2.imprint","INTERSECT",VERTEX,{"derivedFrom":[subQ1,subQ4]});Q44=makeQuery(id+"F2.imprint","IMPRINT",FACE,{"disambiguationData":[TD([[makeQuery(id+"F2.imprint","IMPRINT",EDGE,{"disambiguationData":[TD([[subQ7,-1.0]])],"derivedFrom":subQ1}),1.0]])]});}
            var Q45;
            {var subQ3=sQuery(id+"F2.wireOp",EDGE,"E219");var subQ7=sQuery(id+"F2.wireOp",EDGE,"E272");var subQ9=makeQuery(id+"F2.imprint","INTERSECT",VERTEX,{"derivedFrom":[subQ3,subQ7]});Q45=makeQuery(id+"F2.imprint","IMPRINT",FACE,{"disambiguationData":[TD([[makeQuery(id+"F2.imprint","IMPRINT",EDGE,{"disambiguationData":[TD([[subQ9,-1.0]])],"derivedFrom":subQ3}),1.0]])]});}
            var Q46;
            {var subQ4=sQuery(id+"F2.wireOp",EDGE,"E265");var subQ6=sQuery(id+"F2.wireOp",EDGE,"E219");var subQ7=makeQuery(id+"F2.imprint","INTERSECT",VERTEX,{"derivedFrom":[subQ6,subQ4]});Q46=makeQuery(id+"F2.imprint","IMPRINT",FACE,{"disambiguationData":[TD([[makeQuery(id+"F2.imprint","IMPRINT",EDGE,{"disambiguationData":[TD([[subQ7,-1.0]])],"derivedFrom":subQ6}),1.0]])]});}
            var Q47;
            {var subQ0=sQuery(id+"F2.wireOp",EDGE,"E265");var subQ3=sQuery(id+"F2.wireOp",EDGE,"E219");var subQ4=makeQuery(id+"F2.imprint","INTERSECT",VERTEX,{"derivedFrom":[subQ3,subQ0]});Q47=makeQuery(id+"F2.imprint","IMPRINT",FACE,{"disambiguationData":[TD([[makeQuery(id+"F2.imprint","IMPRINT",EDGE,{"disambiguationData":[TD([[subQ4,-1.0]])],"derivedFrom":subQ3}),-1.0]])]});}
            var Q48;
            {var subQ3=sQuery(id+"F2.wireOp",EDGE,"E219");var subQ5=sQuery(id+"F2.wireOp",EDGE,"E267");var subQ7=makeQuery(id+"F2.imprint","INTERSECT",VERTEX,{"derivedFrom":[subQ3,subQ5]});Q48=makeQuery(id+"F2.imprint","IMPRINT",FACE,{"disambiguationData":[TD([[makeQuery(id+"F2.imprint","IMPRINT",EDGE,{"disambiguationData":[TD([[subQ7,-1.0]])],"derivedFrom":subQ3}),1.0]])]});}
            var Q49;
            {var subQ0=sQuery(id+"F2.wireOp",EDGE,"E267");var subQ1=sQuery(id+"F2.wireOp",EDGE,"E219");var subQ2=makeQuery(id+"F2.imprint","INTERSECT",VERTEX,{"derivedFrom":[subQ1,subQ0]});Q49=makeQuery(id+"F2.imprint","IMPRINT",FACE,{"disambiguationData":[TD([[makeQuery(id+"F2.imprint","IMPRINT",EDGE,{"disambiguationData":[TD([[subQ2,-1.0]])],"derivedFrom":subQ1}),-1.0]])]});}
            var Q50;
            {var subQ0=sQuery(id+"F2.wireOp",EDGE,"E263");var subQ1=sQuery(id+"F2.wireOp",EDGE,"E219");var subQ2=makeQuery(id+"F2.imprint","INTERSECT",VERTEX,{"derivedFrom":[subQ1,subQ0]});Q50=makeQuery(id+"F2.imprint","IMPRINT",FACE,{"disambiguationData":[TD([[makeQuery(id+"F2.imprint","IMPRINT",EDGE,{"disambiguationData":[TD([[subQ2,-1.0]])],"derivedFrom":subQ1}),1.0]])]});}
            var Q51;
            {var subQ0=sQuery(id+"F2.wireOp",EDGE,"E263");var subQ6=sQuery(id+"F2.wireOp",EDGE,"E219");var subQ8=makeQuery(id+"F2.imprint","INTERSECT",VERTEX,{"derivedFrom":[subQ6,subQ0]});Q51=makeQuery(id+"F2.imprint","IMPRINT",FACE,{"disambiguationData":[TD([[makeQuery(id+"F2.imprint","IMPRINT",EDGE,{"disambiguationData":[TD([[subQ8,-1.0]])],"derivedFrom":subQ6}),-1.0]])]});}
            var Q52;
            {var subQ4=sQuery(id+"F2.wireOp",EDGE,"E262");var subQ6=sQuery(id+"F2.wireOp",EDGE,"E219");var subQ7=makeQuery(id+"F2.imprint","INTERSECT",VERTEX,{"derivedFrom":[subQ6,subQ4]});Q52=makeQuery(id+"F2.imprint","IMPRINT",FACE,{"disambiguationData":[TD([[makeQuery(id+"F2.imprint","IMPRINT",EDGE,{"disambiguationData":[TD([[subQ7,-1.0]])],"derivedFrom":subQ6}),-1.0]])]});}
            var Q53;
            {var subQ0=sQuery(id+"F2.wireOp",EDGE,"E262");var subQ3=sQuery(id+"F2.wireOp",EDGE,"E219");var subQ4=makeQuery(id+"F2.imprint","INTERSECT",VERTEX,{"derivedFrom":[subQ3,subQ0]});Q53=makeQuery(id+"F2.imprint","IMPRINT",FACE,{"disambiguationData":[TD([[makeQuery(id+"F2.imprint","IMPRINT",EDGE,{"disambiguationData":[TD([[subQ4,-1.0]])],"derivedFrom":subQ3}),1.0]])]});}
            var Q54;
            {var subQ0=sQuery(id+"F2.wireOp",EDGE,"E272");var subQ1=sQuery(id+"F2.wireOp",EDGE,"E236.bottom");var subQ2=makeQuery(id+"F2.imprint","INTERSECT",VERTEX,{"derivedFrom":[subQ1,subQ0]});Q54=makeQuery(id+"F2.imprint","IMPRINT",FACE,{"disambiguationData":[TD([[makeQuery(id+"F2.imprint","IMPRINT",EDGE,{"disambiguationData":[TD([[subQ2,-1.0]])],"derivedFrom":subQ1}),-1.0]])]});}
            var Q55;
            {var subQ0=sQuery(id+"F2.wireOp",EDGE,"E273");var subQ1=sQuery(id+"F2.wireOp",EDGE,"E236.left");var subQ2=makeQuery(id+"F2.imprint","INTERSECT",VERTEX,{"derivedFrom":[subQ1,subQ0]});Q55=makeQuery(id+"F2.imprint","IMPRINT",FACE,{"disambiguationData":[TD([[makeQuery(id+"F2.imprint","IMPRINT",EDGE,{"disambiguationData":[TD([[subQ2,-1.0]])],"derivedFrom":subQ1}),1.0]])]});}
            var Q56;
            {var subQ0=sQuery(id+"F2.wireOp",EDGE,"E272");var subQ1=sQuery(id+"F2.wireOp",EDGE,"E236.right");var subQ2=makeQuery(id+"F2.imprint","INTERSECT",VERTEX,{"derivedFrom":[subQ1,subQ0]});Q56=makeQuery(id+"F2.imprint","IMPRINT",FACE,{"disambiguationData":[TD([[makeQuery(id+"F2.imprint","IMPRINT",EDGE,{"disambiguationData":[TD([[subQ2,1.0]])],"derivedFrom":subQ1}),-1.0]])]});}
            var Q57;
            {var subQ0=sQuery(id+"F2.wireOp",EDGE,"E273");var subQ1=sQuery(id+"F2.wireOp",EDGE,"E236.top");var subQ2=makeQuery(id+"F2.imprint","INTERSECT",VERTEX,{"derivedFrom":[subQ1,subQ0]});Q57=makeQuery(id+"F2.imprint","IMPRINT",FACE,{"disambiguationData":[TD([[makeQuery(id+"F2.imprint","IMPRINT",EDGE,{"disambiguationData":[TD([[subQ2,1.0]])],"derivedFrom":subQ1}),1.0]])]});}
            var Q58;
            {var subQ0=sQuery(id+"F2.wireOp",EDGE,"E269");var subQ1=sQuery(id+"F2.wireOp",EDGE,"E235.bottom");var subQ2=makeQuery(id+"F2.imprint","INTERSECT",VERTEX,{"derivedFrom":[subQ1,subQ0]});Q58=makeQuery(id+"F2.imprint","IMPRINT",FACE,{"disambiguationData":[TD([[makeQuery(id+"F2.imprint","IMPRINT",EDGE,{"disambiguationData":[TD([[subQ2,1.0]])],"derivedFrom":subQ1}),-1.0]])]});}
            var Q59;
            {var subQ0=sQuery(id+"F2.wireOp",EDGE,"E270");var subQ1=sQuery(id+"F2.wireOp",EDGE,"E235.right");var subQ2=makeQuery(id+"F2.imprint","INTERSECT",VERTEX,{"derivedFrom":[subQ1,subQ0]});Q59=makeQuery(id+"F2.imprint","IMPRINT",FACE,{"disambiguationData":[TD([[makeQuery(id+"F2.imprint","IMPRINT",EDGE,{"disambiguationData":[TD([[subQ2,-1.0]])],"derivedFrom":subQ1}),-1.0]])]});}
            var Q60;
            {var subQ0=sQuery(id+"F2.wireOp",EDGE,"E269");var subQ1=sQuery(id+"F2.wireOp",EDGE,"E235.left");var subQ2=makeQuery(id+"F2.imprint","INTERSECT",VERTEX,{"derivedFrom":[subQ1,subQ0]});Q60=makeQuery(id+"F2.imprint","IMPRINT",FACE,{"disambiguationData":[TD([[makeQuery(id+"F2.imprint","IMPRINT",EDGE,{"disambiguationData":[TD([[subQ2,1.0]])],"derivedFrom":subQ1}),1.0]])]});}
            var Q61;
            {var subQ0=sQuery(id+"F2.wireOp",EDGE,"E270");var subQ1=sQuery(id+"F2.wireOp",EDGE,"E235.top");var subQ2=makeQuery(id+"F2.imprint","INTERSECT",VERTEX,{"derivedFrom":[subQ1,subQ0]});Q61=makeQuery(id+"F2.imprint","IMPRINT",FACE,{"disambiguationData":[TD([[makeQuery(id+"F2.imprint","IMPRINT",EDGE,{"disambiguationData":[TD([[subQ2,-1.0]])],"derivedFrom":subQ1}),1.0]])]});}
            var Q62;
            {var subQ0=sQuery(id+"F2.wireOp",EDGE,"E267");var subQ1=sQuery(id+"F2.wireOp",EDGE,"E237.left");var subQ2=makeQuery(id+"F2.imprint","INTERSECT",VERTEX,{"derivedFrom":[subQ1,subQ0]});Q62=makeQuery(id+"F2.imprint","IMPRINT",FACE,{"disambiguationData":[TD([[makeQuery(id+"F2.imprint","IMPRINT",EDGE,{"disambiguationData":[TD([[subQ2,-1.0]])],"derivedFrom":subQ1}),-1.0]])]});}
            var Q63;
            {var subQ0=sQuery(id+"F2.wireOp",EDGE,"E266");var subQ1=sQuery(id+"F2.wireOp",EDGE,"E237.bottom");var subQ2=makeQuery(id+"F2.imprint","INTERSECT",VERTEX,{"derivedFrom":[subQ1,subQ0]});Q63=makeQuery(id+"F2.imprint","IMPRINT",FACE,{"disambiguationData":[TD([[makeQuery(id+"F2.imprint","IMPRINT",EDGE,{"disambiguationData":[TD([[subQ2,-1.0]])],"derivedFrom":subQ1}),1.0]])]});}
            var Q64;
            {var subQ0=sQuery(id+"F2.wireOp",EDGE,"E267");var subQ1=sQuery(id+"F2.wireOp",EDGE,"E237.top");var subQ2=makeQuery(id+"F2.imprint","INTERSECT",VERTEX,{"derivedFrom":[subQ1,subQ0]});Q64=makeQuery(id+"F2.imprint","IMPRINT",FACE,{"disambiguationData":[TD([[makeQuery(id+"F2.imprint","IMPRINT",EDGE,{"disambiguationData":[TD([[subQ2,1.0]])],"derivedFrom":subQ1}),-1.0]])]});}
            var Q65;
            {var subQ0=sQuery(id+"F2.wireOp",EDGE,"E266");var subQ1=sQuery(id+"F2.wireOp",EDGE,"E237.right");var subQ2=makeQuery(id+"F2.imprint","INTERSECT",VERTEX,{"derivedFrom":[subQ1,subQ0]});Q65=makeQuery(id+"F2.imprint","IMPRINT",FACE,{"disambiguationData":[TD([[makeQuery(id+"F2.imprint","IMPRINT",EDGE,{"disambiguationData":[TD([[subQ2,1.0]])],"derivedFrom":subQ1}),1.0]])]});}
            var Q66;
            {var subQ0=sQuery(id+"F2.wireOp",EDGE,"E263");var subQ1=sQuery(id+"F2.wireOp",EDGE,"E238.left");var subQ2=makeQuery(id+"F2.imprint","INTERSECT",VERTEX,{"derivedFrom":[subQ1,subQ0]});Q66=makeQuery(id+"F2.imprint","IMPRINT",FACE,{"disambiguationData":[TD([[makeQuery(id+"F2.imprint","IMPRINT",EDGE,{"disambiguationData":[TD([[subQ2,1.0]])],"derivedFrom":subQ1}),-1.0]])]});}
            var Q67;
            {var subQ0=sQuery(id+"F2.wireOp",EDGE,"E264");var subQ1=sQuery(id+"F2.wireOp",EDGE,"E238.top");var subQ2=makeQuery(id+"F2.imprint","INTERSECT",VERTEX,{"derivedFrom":[subQ1,subQ0]});Q67=makeQuery(id+"F2.imprint","IMPRINT",FACE,{"disambiguationData":[TD([[makeQuery(id+"F2.imprint","IMPRINT",EDGE,{"disambiguationData":[TD([[subQ2,-1.0]])],"derivedFrom":subQ1}),-1.0]])]});}
            var Q68;
            {var subQ0=sQuery(id+"F2.wireOp",EDGE,"E263");var subQ1=sQuery(id+"F2.wireOp",EDGE,"E238.bottom");var subQ2=makeQuery(id+"F2.imprint","INTERSECT",VERTEX,{"derivedFrom":[subQ1,subQ0]});Q68=makeQuery(id+"F2.imprint","IMPRINT",FACE,{"disambiguationData":[TD([[makeQuery(id+"F2.imprint","IMPRINT",EDGE,{"disambiguationData":[TD([[subQ2,1.0]])],"derivedFrom":subQ1}),1.0]])]});}
            var Q69;
            {var subQ0=sQuery(id+"F2.wireOp",EDGE,"E264");var subQ1=sQuery(id+"F2.wireOp",EDGE,"E238.right");var subQ2=makeQuery(id+"F2.imprint","INTERSECT",VERTEX,{"derivedFrom":[subQ1,subQ0]});Q69=makeQuery(id+"F2.imprint","IMPRINT",FACE,{"disambiguationData":[TD([[makeQuery(id+"F2.imprint","IMPRINT",EDGE,{"disambiguationData":[TD([[subQ2,-1.0]])],"derivedFrom":subQ1}),1.0]])]});}
            var Q70;
            Q70=makeQuery(id+"F2.imprint","IMPRINT",FACE,{"disambiguationData":[TD([[makeQuery(id+"F2.imprint","IMPRINT",EDGE,{"derivedFrom":sQuery(id+"F2.wireOp",EDGE,"E335")}),-1.0]])]});
            var Q71;
            {var subQ0=sQuery(id+"F2.wireOp",EDGE,"E334");var subQ1=sQuery(id+"F2.wireOp",EDGE,"E238.top");var subQ2=makeQuery(id+"F2.imprint","INTERSECT",VERTEX,{"disambiguationData":[OD(0.0)],"derivedFrom":[subQ1,subQ0]});Q71=makeQuery(id+"F2.imprint","IMPRINT",FACE,{"disambiguationData":[TD([[makeQuery(id+"F2.imprint","IMPRINT",EDGE,{"disambiguationData":[TD([[subQ2,-1.0]])],"derivedFrom":subQ1}),-1.0]])]});}
            var Q72;
            {var subQ0=sQuery(id+"F2.wireOp",EDGE,"E334");var subQ1=sQuery(id+"F2.wireOp",EDGE,"E238.top");var subQ2=makeQuery(id+"F2.imprint","INTERSECT",VERTEX,{"disambiguationData":[OD(1.0)],"derivedFrom":[subQ1,subQ0]});Q72=makeQuery(id+"F2.imprint","IMPRINT",FACE,{"disambiguationData":[TD([[makeQuery(id+"F2.imprint","IMPRINT",EDGE,{"disambiguationData":[TD([[subQ2,-1.0]])],"derivedFrom":subQ1}),-1.0]])]});}
            var Q73;
            {var subQ0=sQuery(id+"F2.wireOp",EDGE,"E336");var subQ1=sQuery(id+"F2.wireOp",EDGE,"E238.top");var subQ2=makeQuery(id+"F2.imprint","INTERSECT",VERTEX,{"derivedFrom":[subQ1,subQ0]});Q73=makeQuery(id+"F2.imprint","IMPRINT",FACE,{"disambiguationData":[TD([[makeQuery(id+"F2.imprint","IMPRINT",EDGE,{"disambiguationData":[TD([[subQ2,-1.0]])],"derivedFrom":subQ1}),-1.0]])]});}
            var Q74;
            Q74=makeQuery(id+"F2.imprint","IMPRINT",FACE,{"disambiguationData":[TD([[makeQuery(id+"F2.imprint","IMPRINT",EDGE,{"derivedFrom":sQuery(id+"F2.wireOp",EDGE,"E215")}),-1.0]])]});
            var Q75;
            Q75=makeQuery(id+"F2.imprint","IMPRINT",FACE,{"disambiguationData":[TD([[makeQuery(id+"F2.imprint","IMPRINT",EDGE,{"derivedFrom":sQuery(id+"F2.wireOp",EDGE,"E341.MirrorC")}),1.0]])]});
            var Q76;
            {var subQ0=sQuery(id+"F2.wireOp",EDGE,"E340.MirrorC");var subQ1=sQuery(id+"F2.wireOp",EDGE,"E214.bottom");var subQ2=makeQuery(id+"F2.imprint","INTERSECT",VERTEX,{"disambiguationData":[OD(0.0)],"derivedFrom":[subQ1,subQ0]});Q76=makeQuery(id+"F2.imprint","IMPRINT",FACE,{"disambiguationData":[TD([[makeQuery(id+"F2.imprint","IMPRINT",EDGE,{"disambiguationData":[TD([[subQ2,-1.0]])],"derivedFrom":subQ1}),-1.0]])]});}
            var Q77;
            {var subQ0=sQuery(id+"F2.wireOp",EDGE,"E340.MirrorC");var subQ1=sQuery(id+"F2.wireOp",EDGE,"E238.bottom");var subQ2=makeQuery(id+"F2.imprint","INTERSECT",VERTEX,{"disambiguationData":[OD(0.0)],"derivedFrom":[subQ1,subQ0]});Q77=makeQuery(id+"F2.imprint","IMPRINT",FACE,{"disambiguationData":[TD([[makeQuery(id+"F2.imprint","IMPRINT",EDGE,{"disambiguationData":[TD([[subQ2,-1.0]])],"derivedFrom":subQ1}),1.0]])]});}
            var Q78;
            {var subQ0=sQuery(id+"F2.wireOp",EDGE,"E345.MirrorC");var subQ1=sQuery(id+"F2.wireOp",EDGE,"E214.bottom");var subQ2=makeQuery(id+"F2.imprint","INTERSECT",VERTEX,{"derivedFrom":[subQ1,subQ0]});Q78=makeQuery(id+"F2.imprint","IMPRINT",FACE,{"disambiguationData":[TD([[makeQuery(id+"F2.imprint","IMPRINT",EDGE,{"disambiguationData":[TD([[subQ2,1.0]])],"derivedFrom":subQ1}),-1.0]])]});}
            var Q79;
            {var subQ0=sQuery(id+"F2.wireOp",EDGE,"E344.MirrorC");var subQ1=sQuery(id+"F2.wireOp",EDGE,"E214.bottom");var subQ2=makeQuery(id+"F2.imprint","INTERSECT",VERTEX,{"derivedFrom":[subQ1,subQ0]});Q79=makeQuery(id+"F2.imprint","IMPRINT",FACE,{"disambiguationData":[TD([[makeQuery(id+"F2.imprint","IMPRINT",EDGE,{"disambiguationData":[TD([[subQ2,-1.0]])],"derivedFrom":subQ1}),-1.0]])]});}
            var Q80;
            {var subQ0=sQuery(id+"F2.wireOp",EDGE,"E343.MirrorC");var subQ1=sQuery(id+"F2.wireOp",EDGE,"E238.bottom");var subQ2=makeQuery(id+"F2.imprint","INTERSECT",VERTEX,{"derivedFrom":[subQ1,subQ0]});Q80=makeQuery(id+"F2.imprint","IMPRINT",FACE,{"disambiguationData":[TD([[makeQuery(id+"F2.imprint","IMPRINT",EDGE,{"disambiguationData":[TD([[subQ2,-1.0]])],"derivedFrom":subQ1}),1.0]])]});}
            var Q81;
            {var subQ0=sQuery(id+"F2.wireOp",EDGE,"E340.MirrorC");var subQ1=sQuery(id+"F2.wireOp",EDGE,"E238.bottom");var subQ2=makeQuery(id+"F2.imprint","INTERSECT",VERTEX,{"disambiguationData":[OD(1.0)],"derivedFrom":[subQ1,subQ0]});Q81=makeQuery(id+"F2.imprint","IMPRINT",FACE,{"disambiguationData":[TD([[makeQuery(id+"F2.imprint","IMPRINT",EDGE,{"disambiguationData":[TD([[subQ2,-1.0]])],"derivedFrom":subQ1}),1.0]])]});}
            extrude(context, id + "F3", {"entities" : qUnion([Q0, Q1, Q2, Q3, Q4, Q5, Q6, Q7, Q8, Q9, Q10, Q11, Q12, Q13, Q14, Q15, Q16, Q17, Q18, Q19, Q20, Q21, Q22, Q23, Q24, Q25, Q26, Q27, Q28, Q29, Q30, Q31, Q32, Q33, Q34, Q35, Q36, Q37, Q38, Q39, Q40, Q41, Q42, Q43, Q44, Q45, Q46, Q47, Q48, Q49, Q50, Q51, Q52, Q53, Q54, Q55, Q56, Q57, Q58, Q59, Q60, Q61, Q62, Q63, Q64, Q65, Q66, Q67, Q68, Q69, Q70, Q71, Q72, Q73, Q74, Q75, Q76, Q77, Q78, Q79, Q80, Q81]), "depth" : 1.5 * mm});
        }
    });
